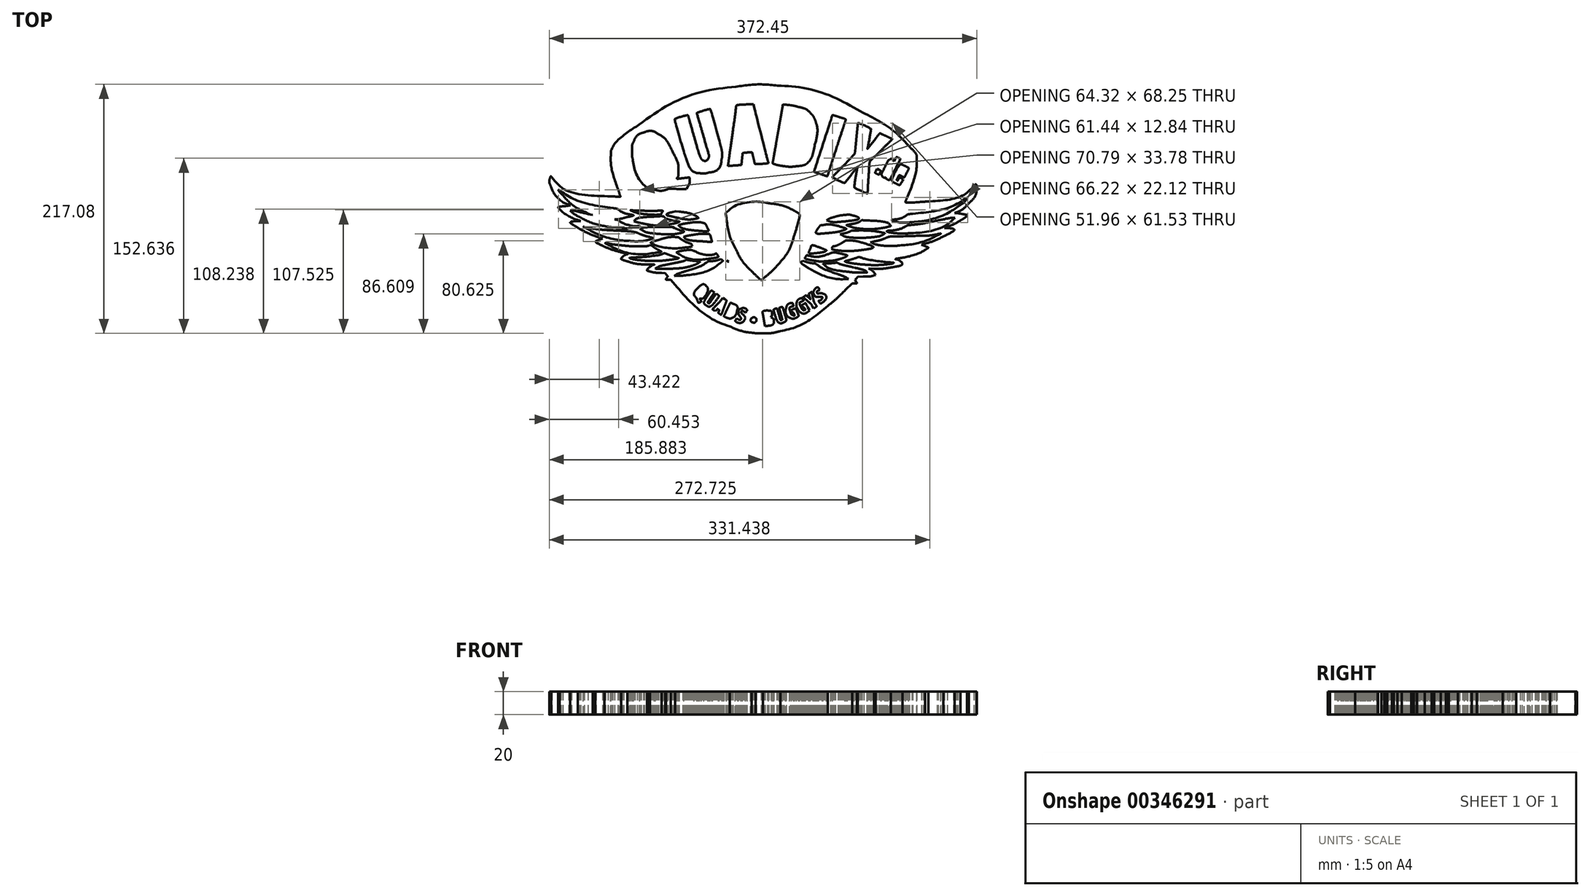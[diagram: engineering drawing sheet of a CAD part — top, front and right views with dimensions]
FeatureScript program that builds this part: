
annotation { "Feature Type Name" : "Feature", "Feature Type Description" : "" }
export const myFeature = defineFeature(function(context is Context, id is Id, definition is map)
    precondition{}
    {
        {
            var Q0;
            Q0=qCreatedBy(makeId("Top.planeOp"),FACE);
            var sketch = newSketch(context, id + "F0", { "sketchPlane" : qUnion([Q0])});
            skFitSpline(sketch, "E0", {"points": [v(-6.57, -108.21) * mm, v(-6.97, -108.16) * mm, v(-8.6, -107.94) * mm, v(-10.17, -107.73) * mm]});
            skFitSpline(sketch, "E1", {"points": [v(-10.17, -107.73) * mm, v(-15.63, -107) * mm, v(-22.77, -104.94) * mm, v(-29.01, -102.3) * mm]});
            skFitSpline(sketch, "E2", {"points": [v(-29.01, -102.3) * mm, v(-44.52, -95.74) * mm, v(-61.29, -82.95) * mm, v(-76.72, -65.93) * mm]});
            skFitSpline(sketch, "E3", {"points": [v(-82.66, -61.55) * mm, v(-83.73, -61.55) * mm, v(-84.68, -61.49) * mm, v(-84.76, -61.4) * mm]});
            skFitSpline(sketch, "E4", {"points": [v(-84.76, -61.4) * mm, v(-84.84, -61.32) * mm, v(-84.54, -60.7) * mm, v(-84.08, -60.03) * mm]});
            skFitSpline(sketch, "E5", {"points": [v(-84.08, -60.03) * mm, v(-83.63, -59.35) * mm, v(-83.25, -58.7) * mm, v(-83.25, -58.6) * mm]});
            skFitSpline(sketch, "E6", {"points": [v(-83.25, -58.6) * mm, v(-83.25, -58.48) * mm, v(-83.74, -57.82) * mm, v(-84.34, -57.12) * mm]});
            skLineSegment(sketch, "E7", {"start": v(-76.72, -65.93) * mm, "end": v(-80.7, -61.55) * mm});
            skLineSegment(sketch, "E8", {"start": v(-80.7, -61.55) * mm, "end": v(-82.66, -61.55) * mm});
            skFitSpline(sketch, "E9", {"points": [v(-88.48, -55.68) * mm, v(-92.46, -55.46) * mm, v(-96.36, -54.96) * mm, v(-98.72, -54.36) * mm]});
            skFitSpline(sketch, "E10", {"points": [v(-98.72, -54.36) * mm, v(-99.76, -54.09) * mm, v(-100.66, -53.83) * mm, v(-100.71, -53.77) * mm]});
            skFitSpline(sketch, "E11", {"points": [v(-100.71, -53.77) * mm, v(-101.28, -53.2) * mm, v(-96.96, -49.12) * mm, v(-95.03, -48.4) * mm]});
            skFitSpline(sketch, "E12", {"points": [v(-95.03, -48.4) * mm, v(-94.78, -48.31) * mm, v(-96.58, -48.22) * mm, v(-99.05, -48.2) * mm]});
            skFitSpline(sketch, "E13", {"points": [v(-99.05, -48.2) * mm, v(-105.73, -48.14) * mm, v(-112.51, -47.22) * mm, v(-118.17, -45.6) * mm]});
            skFitSpline(sketch, "E14", {"points": [v(-118.17, -45.6) * mm, v(-120.5, -44.92) * mm, v(-123.81, -43.47) * mm, v(-123.81, -43.12) * mm]});
            skFitSpline(sketch, "E15", {"points": [v(-123.81, -43.12) * mm, v(-123.81, -43) * mm, v(-123.3, -42.4) * mm, v(-122.65, -41.8) * mm]});
            skFitSpline(sketch, "E16", {"points": [v(-122.65, -41.8) * mm, v(-121.48, -40.72) * mm, v(-120.13, -39.9) * mm, v(-118.57, -39.37) * mm]});
            skFitSpline(sketch, "E17", {"points": [v(-118.57, -39.37) * mm, v(-117.75, -39.08) * mm, v(-117.81, -39.06) * mm, v(-121.43, -38.16) * mm]});
            skFitSpline(sketch, "E18", {"points": [v(-121.43, -38.16) * mm, v(-127.3, -36.7) * mm, v(-133.67, -34.6) * mm, v(-138.21, -32.64) * mm]});
            skFitSpline(sketch, "E19", {"points": [v(-138.21, -32.64) * mm, v(-141.82, -31.08) * mm, v(-146.19, -28.36) * mm, v(-145.73, -27.96) * mm]});
            skFitSpline(sketch, "E20", {"points": [v(-145.73, -27.96) * mm, v(-145.62, -27.86) * mm, v(-144.25, -27.32) * mm, v(-142.68, -26.75) * mm]});
            skLineSegment(sketch, "E21", {"start": v(-84.34, -57.12) * mm, "end": v(-85.42, -55.85) * mm});
            skLineSegment(sketch, "E22", {"start": v(-85.42, -55.85) * mm, "end": v(-88.48, -55.68) * mm});
            skFitSpline(sketch, "E23", {"points": [v(-143.16, -24.6) * mm, v(-145, -23.97) * mm, v(-147.36, -23.12) * mm, v(-148.41, -22.7) * mm]});
            skFitSpline(sketch, "E24", {"points": [v(-148.41, -22.7) * mm, v(-151.53, -21.43) * mm, v(-158.78, -17.84) * mm, v(-161.5, -16.2) * mm]});
            skFitSpline(sketch, "E25", {"points": [v(-161.5, -16.2) * mm, v(-165.45, -13.82) * mm, v(-168.13, -11.68) * mm, v(-167.68, -11.26) * mm]});
            skFitSpline(sketch, "E26", {"points": [v(-167.68, -11.26) * mm, v(-167.32, -10.93) * mm, v(-165.1, -10.61) * mm, v(-162.33, -10.5) * mm]});
            skLineSegment(sketch, "E27", {"start": v(-142.68, -26.75) * mm, "end": v(-139.83, -25.72) * mm});
            skLineSegment(sketch, "E28", {"start": v(-139.83, -25.72) * mm, "end": v(-143.16, -24.6) * mm});
            skFitSpline(sketch, "E29", {"points": [v(-160.17, -9.94) * mm, v(-165.53, -8.08) * mm, v(-174.1, -3.1) * mm, v(-177.45, 0.1) * mm]});
            skFitSpline(sketch, "E30", {"points": [v(-177.45, 0.1) * mm, v(-178.05, 0.67) * mm, v(-178.53, 1.21) * mm, v(-178.53, 1.31) * mm]});
            skFitSpline(sketch, "E31", {"points": [v(-178.53, 1.31) * mm, v(-178.53, 1.66) * mm, v(-173.52, 2.57) * mm, v(-169.82, 2.89) * mm]});
            skLineSegment(sketch, "E32", {"start": v(-162.33, -10.5) * mm, "end": v(-158.97, -10.36) * mm});
            skLineSegment(sketch, "E33", {"start": v(-158.97, -10.36) * mm, "end": v(-160.17, -9.94) * mm});
            skFitSpline(sketch, "E34", {"points": [v(-169.43, 3.76) * mm, v(-174.96, 6.37) * mm, v(-182.09, 13.53) * mm, v(-184.53, 18.93) * mm]});
            skFitSpline(sketch, "E35", {"points": [v(-184.53, 18.93) * mm, v(-185.96, 22.06) * mm, v(-186.33, 25.01) * mm, v(-185.6, 27.44) * mm]});
            skFitSpline(sketch, "E36", {"points": [v(-185.6, 27.44) * mm, v(-185.4, 28.13) * mm, v(-185.15, 28.69) * mm, v(-185.05, 28.69) * mm]});
            skFitSpline(sketch, "E37", {"points": [v(-185.05, 28.69) * mm, v(-184.95, 28.69) * mm, v(-184.45, 28.25) * mm, v(-183.92, 27.7) * mm]});
            skFitSpline(sketch, "E38", {"points": [v(-183.92, 27.7) * mm, v(-174.68, 18.14) * mm, v(-157.86, 12.71) * mm, v(-132.7, 11.17) * mm]});
            skFitSpline(sketch, "E39", {"points": [v(-132.7, 11.17) * mm, v(-130.52, 11.04) * mm, v(-127.72, 10.93) * mm, v(-126.49, 10.93) * mm]});
            skFitSpline(sketch, "E40", {"points": [v(-126.49, 10.93) * mm, v(-124.44, 10.93) * mm, v(-124.26, 10.96) * mm, v(-124.43, 11.35) * mm]});
            skFitSpline(sketch, "E41", {"points": [v(-124.43, 11.35) * mm, v(-124.53, 11.58) * mm, v(-125.51, 14.41) * mm, v(-126.6, 17.65) * mm]});
            skFitSpline(sketch, "E42", {"points": [v(-126.6, 17.65) * mm, v(-130.6, 29.45) * mm, v(-132.7, 39.76) * mm, v(-132.7, 47.68) * mm]});
            skFitSpline(sketch, "E43", {"points": [v(-132.7, 47.68) * mm, v(-132.7, 50.58) * mm, v(-132.66, 50.78) * mm, v(-131.98, 52.07) * mm]});
            skFitSpline(sketch, "E44", {"points": [v(-131.98, 52.07) * mm, v(-129.25, 57.27) * mm, v(-119.8, 65.82) * mm, v(-108.21, 73.56) * mm]});
            skFitSpline(sketch, "E45", {"points": [v(-108.21, 73.56) * mm, v(-82.39, 90.84) * mm, v(-52.34, 102.6) * mm, v(-23.61, 106.67) * mm]});
            skFitSpline(sketch, "E46", {"points": [v(-23.61, 106.67) * mm, v(-11.44, 108.4) * mm, v(0.36, 108.71) * mm, v(12.63, 107.65) * mm]});
            skFitSpline(sketch, "E47", {"points": [v(12.63, 107.65) * mm, v(35.47, 105.67) * mm, v(61.48, 97.6) * mm, v(84.5, 85.35) * mm]});
            skFitSpline(sketch, "E48", {"points": [v(84.5, 85.35) * mm, v(101.82, 76.14) * mm, v(116.2, 65.93) * mm, v(126.16, 55.77) * mm]});
            skFitSpline(sketch, "E49", {"points": [v(126.16, 55.77) * mm, v(131.6, 50.23) * mm, v(133.7, 46.98) * mm, v(133.7, 44.15) * mm]});
            skFitSpline(sketch, "E50", {"points": [v(133.7, 44.15) * mm, v(133.7, 36.24) * mm, v(130.49, 23.07) * mm, v(125.46, 10.4) * mm]});
            skFitSpline(sketch, "E51", {"points": [v(125.46, 10.4) * mm, v(124.58, 8.2) * mm, v(123.87, 6.31) * mm, v(123.87, 6.22) * mm]});
            skFitSpline(sketch, "E52", {"points": [v(123.87, 6.22) * mm, v(123.87, 5.94) * mm, v(138.54, 6.32) * mm, v(143.3, 6.72) * mm]});
            skFitSpline(sketch, "E53", {"points": [v(143.3, 6.72) * mm, v(162.32, 8.32) * mm, v(175.28, 12.72) * mm, v(183.56, 20.38) * mm]});
            skFitSpline(sketch, "E54", {"points": [v(183.56, 20.38) * mm, v(184.38, 21.14) * mm, v(185.15, 21.7) * mm, v(185.28, 21.62) * mm]});
            skFitSpline(sketch, "E55", {"points": [v(185.28, 21.62) * mm, v(185.7, 21.36) * mm, v(186.09, 18.79) * mm, v(185.93, 17.26) * mm]});
            skFitSpline(sketch, "E56", {"points": [v(185.93, 17.26) * mm, v(185.53, 13.36) * mm, v(183.18, 9.18) * mm, v(179.01, 4.95) * mm]});
            skFitSpline(sketch, "E57", {"points": [v(179.01, 4.95) * mm, v(175.48, 1.38) * mm, v(171.2, -1.7) * mm, v(168.17, -2.81) * mm]});
            skLineSegment(sketch, "E58", {"start": v(-169.82, 2.89) * mm, "end": v(-167.95, 3.05) * mm});
            skLineSegment(sketch, "E59", {"start": v(-167.95, 3.05) * mm, "end": v(-169.43, 3.76) * mm});
            skFitSpline(sketch, "E60", {"points": [v(168.7, -3.52) * mm, v(169.79, -3.6) * mm, v(171.3, -3.8) * mm, v(172.05, -3.96) * mm]});
            skFitSpline(sketch, "E61", {"points": [v(172.05, -3.96) * mm, v(175.1, -4.56) * mm, v(177.63, -5.2) * mm, v(177.63, -5.37) * mm]});
            skFitSpline(sketch, "E62", {"points": [v(177.63, -5.37) * mm, v(177.63, -5.87) * mm, v(174.88, -8.01) * mm, v(171.99, -9.77) * mm]});
            skFitSpline(sketch, "E63", {"points": [v(171.99, -9.77) * mm, v(167.65, -12.41) * mm, v(164.93, -13.73) * mm, v(160.27, -15.48) * mm]});
            skLineSegment(sketch, "E64", {"start": v(168.17, -2.81) * mm, "end": v(166.7, -3.35) * mm});
            skLineSegment(sketch, "E65", {"start": v(166.7, -3.35) * mm, "end": v(168.7, -3.52) * mm});
            skFitSpline(sketch, "E66", {"points": [v(160.52, -16.52) * mm, v(163.15, -16.68) * mm, v(165.78, -17.2) * mm, v(166.23, -17.66) * mm]});
            skFitSpline(sketch, "E67", {"points": [v(166.23, -17.66) * mm, v(166.76, -18.2) * mm, v(162.4, -21.1) * mm, v(157, -23.77) * mm]});
            skFitSpline(sketch, "E68", {"points": [v(157, -23.77) * mm, v(151.4, -26.55) * mm, v(145.67, -28.76) * mm, v(139.48, -30.53) * mm]});
            skLineSegment(sketch, "E69", {"start": v(160.27, -15.48) * mm, "end": v(157.91, -16.36) * mm});
            skLineSegment(sketch, "E70", {"start": v(157.91, -16.36) * mm, "end": v(160.52, -16.52) * mm});
            skFitSpline(sketch, "E71", {"points": [v(140.8, -32.14) * mm, v(142.38, -32.79) * mm, v(143.72, -33.36) * mm, v(143.79, -33.42) * mm]});
            skFitSpline(sketch, "E72", {"points": [v(143.79, -33.42) * mm, v(143.98, -33.58) * mm, v(142.58, -34.63) * mm, v(140.92, -35.57) * mm]});
            skFitSpline(sketch, "E73", {"points": [v(140.92, -35.57) * mm, v(136.46, -38.1) * mm, v(126, -41.44) * mm, v(117.82, -42.96) * mm]});
            skFitSpline(sketch, "E74", {"points": [v(117.82, -42.96) * mm, v(115.47, -43.4) * mm, v(115.15, -43.6) * mm, v(116.36, -43.9) * mm]});
            skFitSpline(sketch, "E75", {"points": [v(116.36, -43.9) * mm, v(117.78, -44.25) * mm, v(121.1, -46.9) * mm, v(121.1, -47.67) * mm]});
            skFitSpline(sketch, "E76", {"points": [v(121.1, -47.67) * mm, v(121.1, -48.47) * mm, v(116.4, -50) * mm, v(111.27, -50.87) * mm]});
            skFitSpline(sketch, "E77", {"points": [v(111.27, -50.87) * mm, v(106.35, -51.7) * mm, v(101.4, -52.04) * mm, v(96.34, -51.9) * mm]});
            skLineSegment(sketch, "E78", {"start": v(139.48, -30.53) * mm, "end": v(137.94, -30.97) * mm});
            skLineSegment(sketch, "E79", {"start": v(137.94, -30.97) * mm, "end": v(140.8, -32.14) * mm});
            skFitSpline(sketch, "E80", {"points": [v(93.19, -52.5) * mm, v(94.6, -53.3) * mm, v(96.87, -55.5) * mm, v(97.53, -56.69) * mm]});
            skLineSegment(sketch, "E81", {"start": v(96.34, -51.9) * mm, "end": v(91.92, -51.78) * mm});
            skLineSegment(sketch, "E82", {"start": v(91.92, -51.78) * mm, "end": v(93.19, -52.5) * mm});
            skFitSpline(sketch, "E83", {"points": [v(96.7, -57.82) * mm, v(94.52, -58.45) * mm, v(92.23, -58.7) * mm, v(87.22, -58.84) * mm]});
            skLineSegment(sketch, "E84", {"start": v(97.53, -56.69) * mm, "end": v(97.96, -57.45) * mm});
            skLineSegment(sketch, "E85", {"start": v(97.96, -57.45) * mm, "end": v(96.7, -57.82) * mm});
            skFitSpline(sketch, "E86", {"points": [v(80.86, -63.01) * mm, v(81.28, -63.78) * mm, v(81.63, -64.46) * mm, v(81.63, -64.54) * mm]});
            skFitSpline(sketch, "E87", {"points": [v(81.63, -64.54) * mm, v(81.63, -64.61) * mm, v(80.68, -64.67) * mm, v(79.53, -64.67) * mm]});
            skLineSegment(sketch, "E88", {"start": v(87.22, -58.84) * mm, "end": v(82.38, -58.98) * mm});
            skLineSegment(sketch, "E89", {"start": v(82.38, -58.98) * mm, "end": v(81.23, -60.3) * mm});
            skLineSegment(sketch, "E90", {"start": v(81.23, -60.3) * mm, "end": v(80.1, -61.63) * mm});
            skLineSegment(sketch, "E91", {"start": v(80.1, -61.63) * mm, "end": v(80.86, -63.01) * mm});
            skFitSpline(sketch, "E92", {"points": [v(71.55, -70.5) * mm, v(65.32, -76.67) * mm, v(61.44, -80.17) * mm, v(56.23, -84.33) * mm]});
            skFitSpline(sketch, "E93", {"points": [v(56.23, -84.33) * mm, v(42.35, -95.39) * mm, v(28.04, -103) * mm, v(14.93, -106.3) * mm]});
            skFitSpline(sketch, "E94", {"points": [v(14.93, -106.3) * mm, v(9.4, -107.7) * mm, v(5.85, -108.16) * mm, v(-0.21, -108.24) * mm]});
            skFitSpline(sketch, "E95", {"points": [v(-0.21, -108.24) * mm, v(-3.32, -108.28) * mm, v(-6.18, -108.27) * mm, v(-6.57, -108.21) * mm]});
            skLineSegment(sketch, "E96", {"start": v(79.53, -64.67) * mm, "end": v(77.43, -64.68) * mm});
            skLineSegment(sketch, "E97", {"start": v(77.43, -64.68) * mm, "end": v(71.55, -70.5) * mm});
            skFitSpline(sketch, "E98", {"points": [v(4.95, -101.6) * mm, v(7.46, -101.13) * mm, v(9.15, -99.57) * mm, v(9.15, -97.73) * mm]});
            skFitSpline(sketch, "E99", {"points": [v(9.15, -97.73) * mm, v(9.15, -96.34) * mm, v(8.5, -95.16) * mm, v(7.47, -94.7) * mm]});
            skLineSegment(sketch, "E100", {"start": v(-6.57, -108.21) * mm, "end": v(-6.57, -108.21) * mm});
            skFitSpline(sketch, "E101", {"points": [v(7.18, -93.47) * mm, v(7.65, -92.78) * mm, v(7.73, -92.41) * mm, v(7.65, -91.36) * mm]});
            skFitSpline(sketch, "E102", {"points": [v(7.65, -91.36) * mm, v(7.5, -89.53) * mm, v(6.58, -88.64) * mm, v(4.69, -88.48) * mm]});
            skFitSpline(sketch, "E103", {"points": [v(4.69, -88.48) * mm, v(3.32, -88.37) * mm, v(0.42, -88.76) * mm, v(-0.2, -89.14) * mm]});
            skFitSpline(sketch, "E104", {"points": [v(-0.2, -89.14) * mm, v(-0.51, -89.34) * mm, v(-0.06, -92.94) * mm, v(1.26, -100.62) * mm]});
            skLineSegment(sketch, "E105", {"start": v(7.47, -94.7) * mm, "end": v(6.6, -94.31) * mm});
            skLineSegment(sketch, "E106", {"start": v(6.6, -94.31) * mm, "end": v(7.18, -93.47) * mm});
            skFitSpline(sketch, "E107", {"points": [v(2.63, -101.99) * mm, v(3.24, -101.9) * mm, v(4.29, -101.74) * mm, v(4.95, -101.6) * mm]});
            skLineSegment(sketch, "E108", {"start": v(1.26, -100.62) * mm, "end": v(1.52, -102.13) * mm});
            skLineSegment(sketch, "E109", {"start": v(1.52, -102.13) * mm, "end": v(2.63, -101.99) * mm});
            skFitSpline(sketch, "E110", {"points": [v(17.64, -98.8) * mm, v(19.8, -97.55) * mm, v(19.91, -95.56) * mm, v(18.16, -89.45) * mm]});
            skFitSpline(sketch, "E111", {"points": [v(18.16, -89.45) * mm, v(17.5, -87.18) * mm, v(16.87, -85.31) * mm, v(16.75, -85.31) * mm]});
            skFitSpline(sketch, "E112", {"points": [v(16.75, -85.31) * mm, v(16.28, -85.31) * mm, v(13.95, -86.08) * mm, v(13.95, -86.23) * mm]});
            skFitSpline(sketch, "E113", {"points": [v(13.95, -86.23) * mm, v(13.95, -86.32) * mm, v(14.53, -88.44) * mm, v(15.24, -90.95) * mm]});
            skFitSpline(sketch, "E114", {"points": [v(15.24, -90.95) * mm, v(16.54, -95.52) * mm, v(16.62, -96.38) * mm, v(15.8, -96.55) * mm]});
            skFitSpline(sketch, "E115", {"points": [v(15.8, -96.55) * mm, v(15.16, -96.67) * mm, v(14.71, -95.65) * mm, v(13.42, -91.17) * mm]});
            skFitSpline(sketch, "E116", {"points": [v(13.42, -91.17) * mm, v(12.74, -88.8) * mm, v(12.14, -86.83) * mm, v(12.1, -86.77) * mm]});
            skFitSpline(sketch, "E117", {"points": [v(12.1, -86.77) * mm, v(11.96, -86.59) * mm, v(9.34, -87.32) * mm, v(9.24, -87.58) * mm]});
            skFitSpline(sketch, "E118", {"points": [v(9.24, -87.58) * mm, v(9.1, -87.95) * mm, v(11.4, -95.83) * mm, v(11.97, -96.96) * mm]});
            skFitSpline(sketch, "E119", {"points": [v(11.97, -96.96) * mm, v(12.53, -98.05) * mm, v(13.32, -98.85) * mm, v(14.19, -99.21) * mm]});
            skFitSpline(sketch, "E120", {"points": [v(14.19, -99.21) * mm, v(14.95, -99.53) * mm, v(16.74, -99.31) * mm, v(17.64, -98.8) * mm]});
            skFitSpline(sketch, "E121", {"points": [v(-18.2, -98.68) * mm, v(-17.5, -98.3) * mm, v(-16.99, -97.8) * mm, v(-16.6, -97.08) * mm]});
            skFitSpline(sketch, "E122", {"points": [v(-16.6, -97.08) * mm, v(-15.66, -95.3) * mm, v(-15.94, -93.78) * mm, v(-17.6, -91.82) * mm]});
            skFitSpline(sketch, "E123", {"points": [v(-17.6, -91.82) * mm, v(-19.17, -89.94) * mm, v(-18.31, -88.63) * mm, v(-16.23, -89.73) * mm]});
            skFitSpline(sketch, "E124", {"points": [v(-14.54, -89.16) * mm, v(-13.94, -88.07) * mm, v(-13.92, -88) * mm, v(-14.33, -87.63) * mm]});
            skFitSpline(sketch, "E125", {"points": [v(-14.33, -87.63) * mm, v(-15.54, -86.54) * mm, v(-18.06, -86.19) * mm, v(-19.57, -86.9) * mm]});
            skFitSpline(sketch, "E126", {"points": [v(-19.57, -86.9) * mm, v(-20.72, -87.45) * mm, v(-21.57, -88.99) * mm, v(-21.57, -90.51) * mm]});
            skFitSpline(sketch, "E127", {"points": [v(-21.57, -90.51) * mm, v(-21.57, -91.52) * mm, v(-21.42, -91.93) * mm, v(-20.63, -93.07) * mm]});
            skFitSpline(sketch, "E128", {"points": [v(-20.63, -93.07) * mm, v(-19.22, -95.07) * mm, v(-19.12, -95.32) * mm, v(-19.41, -95.87) * mm]});
            skFitSpline(sketch, "E129", {"points": [v(-19.41, -95.87) * mm, v(-19.77, -96.54) * mm, v(-20.94, -96.5) * mm, v(-22.2, -95.75) * mm]});
            skLineSegment(sketch, "E130", {"start": v(-16.23, -89.73) * mm, "end": v(-15.18, -90.3) * mm});
            skLineSegment(sketch, "E131", {"start": v(-15.18, -90.3) * mm, "end": v(-14.54, -89.16) * mm});
            skFitSpline(sketch, "E132", {"points": [v(-23.84, -96.32) * mm, v(-24.43, -97.48) * mm, v(-24.43, -97.5) * mm, v(-23.97, -97.92) * mm]});
            skFitSpline(sketch, "E133", {"points": [v(-23.97, -97.92) * mm, v(-23.34, -98.49) * mm, v(-21.19, -99.21) * mm, v(-20.11, -99.22) * mm]});
            skFitSpline(sketch, "E134", {"points": [v(-20.11, -99.22) * mm, v(-19.64, -99.23) * mm, v(-18.78, -98.98) * mm, v(-18.2, -98.68) * mm]});
            skLineSegment(sketch, "E135", {"start": v(-22.2, -95.75) * mm, "end": v(-23.24, -95.14) * mm});
            skLineSegment(sketch, "E136", {"start": v(-23.24, -95.14) * mm, "end": v(-23.84, -96.32) * mm});
            skFitSpline(sketch, "E137", {"points": [v(-6.71, -98.37) * mm, v(-6.08, -97.84) * mm, v(-5.97, -97.6) * mm, v(-5.97, -96.59) * mm]});
            skFitSpline(sketch, "E138", {"points": [v(-5.97, -96.59) * mm, v(-5.97, -95.62) * mm, v(-6.08, -95.34) * mm, v(-6.6, -94.93) * mm]});
            skFitSpline(sketch, "E139", {"points": [v(-6.6, -94.93) * mm, v(-7.31, -94.37) * mm, v(-8.75, -94.27) * mm, v(-9.36, -94.74) * mm]});
            skFitSpline(sketch, "E140", {"points": [v(-9.36, -94.74) * mm, v(-10.72, -95.8) * mm, v(-10.52, -98.14) * mm, v(-9, -98.75) * mm]});
            skFitSpline(sketch, "E141", {"points": [v(-9, -98.75) * mm, v(-8.11, -99.12) * mm, v(-7.47, -99.01) * mm, v(-6.71, -98.37) * mm]});
            skFitSpline(sketch, "E142", {"points": [v(-26.9, -94.74) * mm, v(-25.3, -93.98) * mm, v(-23.31, -90.9) * mm, v(-22.78, -88.32) * mm]});
            skFitSpline(sketch, "E143", {"points": [v(-22.78, -88.32) * mm, v(-22.24, -85.76) * mm, v(-23.35, -83.9) * mm, v(-26.25, -82.52) * mm]});
            skFitSpline(sketch, "E144", {"points": [v(-26.25, -82.52) * mm, v(-27.17, -82.07) * mm, v(-28.1, -81.71) * mm, v(-28.31, -81.71) * mm]});
            skFitSpline(sketch, "E145", {"points": [v(-28.31, -81.71) * mm, v(-28.58, -81.71) * mm, v(-29.53, -83.42) * mm, v(-31.42, -87.33) * mm]});
            skFitSpline(sketch, "E146", {"points": [v(-31.42, -87.33) * mm, v(-32.9, -90.43) * mm, v(-34.14, -93.04) * mm, v(-34.15, -93.15) * mm]});
            skFitSpline(sketch, "E147", {"points": [v(-34.15, -93.15) * mm, v(-34.18, -93.44) * mm, v(-31.72, -94.72) * mm, v(-30.45, -95.07) * mm]});
            skFitSpline(sketch, "E148", {"points": [v(-30.45, -95.07) * mm, v(-29.25, -95.4) * mm, v(-28.1, -95.3) * mm, v(-26.9, -94.74) * mm]});
            skFitSpline(sketch, "E149", {"points": [v(28.91, -94.56) * mm, v(29.66, -94.18) * mm, v(30.39, -93.74) * mm, v(30.52, -93.57) * mm]});
            skFitSpline(sketch, "E150", {"points": [v(30.52, -93.57) * mm, v(30.82, -93.21) * mm, v(28.18, -86.75) * mm, v(27.74, -86.75) * mm]});
            skFitSpline(sketch, "E151", {"points": [v(27.74, -86.75) * mm, v(27.47, -86.75) * mm, v(24.74, -87.89) * mm, v(24.54, -88.08) * mm]});
            skFitSpline(sketch, "E152", {"points": [v(24.54, -88.08) * mm, v(24.5, -88.13) * mm, v(24.65, -88.66) * mm, v(24.88, -89.27) * mm]});
            skFitSpline(sketch, "E153", {"points": [v(24.88, -89.27) * mm, v(25.23, -90.2) * mm, v(25.39, -90.36) * mm, v(25.8, -90.26) * mm]});
            skFitSpline(sketch, "E154", {"points": [v(25.8, -90.26) * mm, v(26.22, -90.15) * mm, v(26.39, -90.32) * mm, v(26.76, -91.23) * mm]});
            skFitSpline(sketch, "E155", {"points": [v(26.76, -91.23) * mm, v(27.29, -92.5) * mm, v(27.04, -92.86) * mm, v(25.9, -92.46) * mm]});
            skFitSpline(sketch, "E156", {"points": [v(25.9, -92.46) * mm, v(24.95, -92.13) * mm, v(23.98, -90.74) * mm, v(23.43, -88.94) * mm]});
            skFitSpline(sketch, "E157", {"points": [v(23.43, -88.94) * mm, v(22.83, -86.93) * mm, v(23.15, -85.76) * mm, v(24.5, -85.07) * mm]});
            skFitSpline(sketch, "E158", {"points": [v(24.5, -85.07) * mm, v(25.02, -84.8) * mm, v(25.61, -84.6) * mm, v(25.82, -84.6) * mm]});
            skFitSpline(sketch, "E159", {"points": [v(25.82, -84.6) * mm, v(26.25, -84.6) * mm, v(26.28, -84.1) * mm, v(25.93, -82.85) * mm]});
            skFitSpline(sketch, "E160", {"points": [v(25.93, -82.85) * mm, v(25.72, -82.1) * mm, v(25.58, -81.95) * mm, v(25.03, -81.95) * mm]});
            skFitSpline(sketch, "E161", {"points": [v(25.03, -81.95) * mm, v(23.18, -81.96) * mm, v(20.67, -84) * mm, v(20.15, -85.91) * mm]});
            skFitSpline(sketch, "E162", {"points": [v(20.15, -85.91) * mm, v(19.33, -88.95) * mm, v(21.23, -93.57) * mm, v(23.85, -94.9) * mm]});
            skFitSpline(sketch, "E163", {"points": [v(23.85, -94.9) * mm, v(25.24, -95.6) * mm, v(27.08, -95.48) * mm, v(28.91, -94.56) * mm]});
            skFitSpline(sketch, "E164", {"points": [v(-34.32, -86.25) * mm, v(-33.12, -83.06) * mm, v(-32.08, -80.23) * mm, v(-32, -79.95) * mm]});
            skFitSpline(sketch, "E165", {"points": [v(-32, -79.95) * mm, v(-31.9, -79.52) * mm, v(-32.15, -79.28) * mm, v(-33.46, -78.52) * mm]});
            skFitSpline(sketch, "E166", {"points": [v(-37.02, -79.72) * mm, v(-42.27, -85.32) * mm, v(-44.13, -87.35) * mm, v(-44.13, -87.47) * mm]});
            skFitSpline(sketch, "E167", {"points": [v(-44.13, -87.47) * mm, v(-44.13, -87.54) * mm, v(-43.58, -87.9) * mm, v(-42.91, -88.28) * mm]});
            skLineSegment(sketch, "E168", {"start": v(-33.46, -78.52) * mm, "end": v(-35.04, -77.6) * mm});
            skLineSegment(sketch, "E169", {"start": v(-35.04, -77.6) * mm, "end": v(-37.02, -79.72) * mm});
            skFitSpline(sketch, "E170", {"points": [v(-40.8, -88.1) * mm, v(-39.79, -87.1) * mm, v(-39.67, -87.08) * mm, v(-38.88, -87.68) * mm]});
            skFitSpline(sketch, "E171", {"points": [v(-38.88, -87.68) * mm, v(-38.31, -88.12) * mm, v(-38.3, -88.13) * mm, v(-38.7, -89.28) * mm]});
            skFitSpline(sketch, "E172", {"points": [v(-38.7, -89.28) * mm, v(-38.92, -89.91) * mm, v(-39.03, -90.5) * mm, v(-38.95, -90.57) * mm]});
            skFitSpline(sketch, "E173", {"points": [v(-38.95, -90.57) * mm, v(-38.73, -90.8) * mm, v(-36.83, -92) * mm, v(-36.67, -92.02) * mm]});
            skFitSpline(sketch, "E174", {"points": [v(-36.67, -92.02) * mm, v(-36.58, -92.03) * mm, v(-35.53, -89.43) * mm, v(-34.32, -86.25) * mm]});
            skLineSegment(sketch, "E175", {"start": v(-42.91, -88.28) * mm, "end": v(-41.69, -88.97) * mm});
            skLineSegment(sketch, "E176", {"start": v(-41.69, -88.97) * mm, "end": v(-40.8, -88.1) * mm});
            skFitSpline(sketch, "E177", {"points": [v(37.6, -90.38) * mm, v(38.14, -90.14) * mm, v(38.97, -89.59) * mm, v(39.46, -89.16) * mm]});
            skFitSpline(sketch, "E178", {"points": [v(38.84, -85.6) * mm, v(38.02, -84.05) * mm, v(37.23, -82.6) * mm, v(37.1, -82.37) * mm]});
            skFitSpline(sketch, "E179", {"points": [v(37.1, -82.37) * mm, v(36.87, -81.99) * mm, v(36.72, -82.02) * mm, v(35.24, -82.8) * mm]});
            skFitSpline(sketch, "E180", {"points": [v(35.24, -82.8) * mm, v(34.35, -83.28) * mm, v(33.63, -83.7) * mm, v(33.63, -83.76) * mm]});
            skFitSpline(sketch, "E181", {"points": [v(33.63, -83.76) * mm, v(33.63, -83.82) * mm, v(33.86, -84.34) * mm, v(34.15, -84.93) * mm]});
            skFitSpline(sketch, "E182", {"points": [v(34.15, -84.93) * mm, v(34.58, -85.82) * mm, v(34.74, -85.97) * mm, v(35.09, -85.78) * mm]});
            skFitSpline(sketch, "E183", {"points": [v(35.09, -85.78) * mm, v(35.43, -85.6) * mm, v(35.62, -85.75) * mm, v(36.13, -86.67) * mm]});
            skFitSpline(sketch, "E184", {"points": [v(36.13, -86.67) * mm, v(36.8, -87.87) * mm, v(36.8, -87.88) * mm, v(36.27, -87.96) * mm]});
            skFitSpline(sketch, "E185", {"points": [v(36.27, -87.96) * mm, v(34.97, -88.14) * mm, v(33.82, -87.2) * mm, v(32.87, -85.2) * mm]});
            skFitSpline(sketch, "E186", {"points": [v(32.87, -85.2) * mm, v(31.72, -82.78) * mm, v(32.02, -81.34) * mm, v(33.84, -80.48) * mm]});
            skFitSpline(sketch, "E187", {"points": [v(33.84, -80.48) * mm, v(34.45, -80.19) * mm, v(34.97, -79.94) * mm, v(35, -79.91) * mm]});
            skFitSpline(sketch, "E188", {"points": [v(35, -79.91) * mm, v(35.07, -79.87) * mm, v(34.33, -77.58) * mm, v(34.2, -77.43) * mm]});
            skFitSpline(sketch, "E189", {"points": [v(34.2, -77.43) * mm, v(34.17, -77.38) * mm, v(33.57, -77.53) * mm, v(32.88, -77.76) * mm]});
            skFitSpline(sketch, "E190", {"points": [v(32.88, -77.76) * mm, v(31.38, -78.26) * mm, v(29.74, -79.8) * mm, v(29.31, -81.1) * mm]});
            skFitSpline(sketch, "E191", {"points": [v(29.31, -81.1) * mm, v(28.86, -82.47) * mm, v(29.1, -84.96) * mm, v(29.83, -86.54) * mm]});
            skFitSpline(sketch, "E192", {"points": [v(29.83, -86.54) * mm, v(30.57, -88.14) * mm, v(31.94, -89.73) * mm, v(33.13, -90.36) * mm]});
            skFitSpline(sketch, "E193", {"points": [v(33.13, -90.36) * mm, v(34.25, -90.95) * mm, v(36.32, -90.96) * mm, v(37.6, -90.38) * mm]});
            skLineSegment(sketch, "E194", {"start": v(39.46, -89.16) * mm, "end": v(40.34, -88.39) * mm});
            skLineSegment(sketch, "E195", {"start": v(40.34, -88.39) * mm, "end": v(38.84, -85.6) * mm});
            skFitSpline(sketch, "E196", {"points": [v(46.17, -85.2) * mm, v(46.4, -85.07) * mm, v(46.59, -84.88) * mm, v(46.59, -84.78) * mm]});
            skFitSpline(sketch, "E197", {"points": [v(46.59, -84.78) * mm, v(46.59, -84.69) * mm, v(46.03, -83.74) * mm, v(45.36, -82.67) * mm]});
            skFitSpline(sketch, "E198", {"points": [v(45.36, -82.67) * mm, v(44.2, -80.86) * mm, v(44.07, -80.48) * mm, v(43.19, -76.5) * mm]});
            skFitSpline(sketch, "E199", {"points": [v(43.19, -76.5) * mm, v(42.67, -74.16) * mm, v(42.22, -72.23) * mm, v(42.2, -72.2) * mm]});
            skFitSpline(sketch, "E200", {"points": [v(42.2, -72.2) * mm, v(42.16, -72.17) * mm, v(41.52, -72.52) * mm, v(40.77, -72.98) * mm]});
            skFitSpline(sketch, "E201", {"points": [v(40.1, -75.67) * mm, v(40.47, -76.68) * mm, v(40.89, -77.79) * mm, v(41.02, -78.13) * mm]});
            skFitSpline(sketch, "E202", {"points": [v(41.02, -78.13) * mm, v(41.2, -78.57) * mm, v(40.74, -78.24) * mm, v(39.42, -76.99) * mm]});
            skFitSpline(sketch, "E203", {"points": [v(39.42, -76.99) * mm, v(38.41, -76.02) * mm, v(37.48, -75.24) * mm, v(37.35, -75.24) * mm]});
            skFitSpline(sketch, "E204", {"points": [v(37.35, -75.24) * mm, v(37.21, -75.24) * mm, v(36.54, -75.6) * mm, v(35.84, -76.05) * mm]});
            skLineSegment(sketch, "E205", {"start": v(40.77, -72.98) * mm, "end": v(39.4, -73.82) * mm});
            skLineSegment(sketch, "E206", {"start": v(39.4, -73.82) * mm, "end": v(40.1, -75.67) * mm});
            skFitSpline(sketch, "E207", {"points": [v(38.06, -79.66) * mm, v(41.2, -82.2) * mm, v(41.66, -82.67) * mm, v(42.77, -84.5) * mm]});
            skLineSegment(sketch, "E208", {"start": v(35.84, -76.05) * mm, "end": v(34.58, -76.85) * mm});
            skLineSegment(sketch, "E209", {"start": v(34.58, -76.85) * mm, "end": v(38.06, -79.66) * mm});
            skFitSpline(sketch, "E210", {"points": [v(44.88, -85.99) * mm, v(45.35, -85.7) * mm, v(45.93, -85.35) * mm, v(46.17, -85.2) * mm]});
            skLineSegment(sketch, "E211", {"start": v(42.77, -84.5) * mm, "end": v(44, -86.51) * mm});
            skLineSegment(sketch, "E212", {"start": v(44, -86.51) * mm, "end": v(44.88, -85.99) * mm});
            skFitSpline(sketch, "E213", {"points": [v(-45.39, -84.38) * mm, v(-44.9, -84.12) * mm, v(-44.26, -83.67) * mm, v(-43.98, -83.36) * mm]});
            skFitSpline(sketch, "E214", {"points": [v(-43.98, -83.36) * mm, v(-42.97, -82.25) * mm, v(-38.4, -75.62) * mm, v(-38.52, -75.43) * mm]});
            skFitSpline(sketch, "E215", {"points": [v(-38.52, -75.43) * mm, v(-38.59, -75.33) * mm, v(-39.14, -74.9) * mm, v(-39.75, -74.48) * mm]});
            skFitSpline(sketch, "E216", {"points": [v(-41.28, -74.25) * mm, v(-41.52, -74.54) * mm, v(-42.8, -76.33) * mm, v(-44.13, -78.23) * mm]});
            skFitSpline(sketch, "E217", {"points": [v(-44.13, -78.23) * mm, v(-46.37, -81.45) * mm, v(-47.13, -82.2) * mm, v(-47.73, -81.83) * mm]});
            skFitSpline(sketch, "E218", {"points": [v(-47.73, -81.83) * mm, v(-48.26, -81.51) * mm, v(-47.92, -80.5) * mm, v(-46.71, -78.74) * mm]});
            skFitSpline(sketch, "E219", {"points": [v(-46.71, -78.74) * mm, v(-46.02, -77.74) * mm, v(-44.78, -75.95) * mm, v(-43.96, -74.77) * mm]});
            skLineSegment(sketch, "E220", {"start": v(-39.75, -74.48) * mm, "end": v(-40.85, -73.72) * mm});
            skLineSegment(sketch, "E221", {"start": v(-40.85, -73.72) * mm, "end": v(-41.28, -74.25) * mm});
            skFitSpline(sketch, "E222", {"points": [v(-43.65, -71.75) * mm, v(-44.3, -71.27) * mm, v(-44.95, -70.94) * mm, v(-45.07, -71.02) * mm]});
            skFitSpline(sketch, "E223", {"points": [v(-45.07, -71.02) * mm, v(-45.49, -71.27) * mm, v(-50.15, -78.1) * mm, v(-50.62, -79.13) * mm]});
            skFitSpline(sketch, "E224", {"points": [v(-50.62, -79.13) * mm, v(-51.57, -81.22) * mm, v(-51.1, -82.85) * mm, v(-49.16, -84.15) * mm]});
            skFitSpline(sketch, "E225", {"points": [v(-49.16, -84.15) * mm, v(-47.94, -84.97) * mm, v(-46.68, -85.04) * mm, v(-45.39, -84.38) * mm]});
            skLineSegment(sketch, "E226", {"start": v(-43.96, -74.77) * mm, "end": v(-42.46, -72.63) * mm});
            skLineSegment(sketch, "E227", {"start": v(-42.46, -72.63) * mm, "end": v(-43.65, -71.75) * mm});
            skFitSpline(sketch, "E228", {"points": [v(51.57, -81.46) * mm, v(52.26, -81.06) * mm, v(53.15, -80.3) * mm, v(53.55, -79.75) * mm]});
            skFitSpline(sketch, "E229", {"points": [v(53.55, -79.75) * mm, v(55, -77.73) * mm, v(54.3, -74.91) * mm, v(52.05, -73.76) * mm]});
            skFitSpline(sketch, "E230", {"points": [v(52.05, -73.76) * mm, v(51.23, -73.35) * mm, v(50.77, -73.28) * mm, v(49.52, -73.38) * mm]});
            skFitSpline(sketch, "E231", {"points": [v(49.52, -73.38) * mm, v(47.6, -73.53) * mm, v(47.1, -73.4) * mm, v(46.91, -72.67) * mm]});
            skFitSpline(sketch, "E232", {"points": [v(46.91, -72.67) * mm, v(46.73, -71.96) * mm, v(47.3, -71.27) * mm, v(48.4, -70.87) * mm]});
            skFitSpline(sketch, "E233", {"points": [v(48.6, -69.43) * mm, v(48.28, -68.8) * mm, v(47.85, -68.27) * mm, v(47.65, -68.27) * mm]});
            skFitSpline(sketch, "E234", {"points": [v(47.65, -68.27) * mm, v(46.77, -68.27) * mm, v(44.92, -69.76) * mm, v(44.28, -70.96) * mm]});
            skFitSpline(sketch, "E235", {"points": [v(44.28, -70.96) * mm, v(43.75, -71.97) * mm, v(43.85, -73.82) * mm, v(44.49, -74.76) * mm]});
            skFitSpline(sketch, "E236", {"points": [v(44.49, -74.76) * mm, v(45.4, -76.12) * mm, v(46.42, -76.55) * mm, v(48.68, -76.56) * mm]});
            skFitSpline(sketch, "E237", {"points": [v(48.68, -76.56) * mm, v(51, -76.56) * mm, v(51.64, -76.92) * mm, v(51.25, -78.03) * mm]});
            skFitSpline(sketch, "E238", {"points": [v(51.25, -78.03) * mm, v(51.06, -78.58) * mm, v(49.8, -79.48) * mm, v(48.73, -79.84) * mm]});
            skFitSpline(sketch, "E239", {"points": [v(48.73, -79.84) * mm, v(48.4, -79.95) * mm, v(49.64, -82.2) * mm, v(50.03, -82.2) * mm]});
            skFitSpline(sketch, "E240", {"points": [v(50.03, -82.2) * mm, v(50.18, -82.19) * mm, v(50.87, -81.86) * mm, v(51.57, -81.46) * mm]});
            skLineSegment(sketch, "E241", {"start": v(48.4, -70.87) * mm, "end": v(49.2, -70.59) * mm});
            skLineSegment(sketch, "E242", {"start": v(49.2, -70.59) * mm, "end": v(48.6, -69.43) * mm});
            skFitSpline(sketch, "E243", {"points": [v(-55.1, -81.2) * mm, v(-54.55, -80.92) * mm, v(-54.05, -80.66) * mm, v(-54, -80.61) * mm]});
            skFitSpline(sketch, "E244", {"points": [v(-54, -80.61) * mm, v(-53.96, -80.57) * mm, v(-54.2, -80.05) * mm, v(-54.55, -79.46) * mm]});
            skFitSpline(sketch, "E245", {"points": [v(-54.55, -79.46) * mm, v(-55.31, -78.15) * mm, v(-55.32, -78.11) * mm, v(-54.6, -78.11) * mm]});
            skFitSpline(sketch, "E246", {"points": [v(-54.6, -78.11) * mm, v(-53.21, -78.11) * mm, v(-50.1, -75.12) * mm, v(-48.9, -72.62) * mm]});
            skFitSpline(sketch, "E247", {"points": [v(-48.9, -72.62) * mm, v(-48.25, -71.3) * mm, v(-48.06, -69.47) * mm, v(-48.46, -68.51) * mm]});
            skFitSpline(sketch, "E248", {"points": [v(-48.46, -68.51) * mm, v(-48.62, -68.11) * mm, v(-49.07, -67.52) * mm, v(-49.46, -67.2) * mm]});
            skFitSpline(sketch, "E249", {"points": [v(-49.46, -67.2) * mm, v(-51.4, -65.56) * mm, v(-53.72, -65.94) * mm, v(-56.25, -68.3) * mm]});
            skFitSpline(sketch, "E250", {"points": [v(-56.25, -68.3) * mm, v(-59.11, -70.98) * mm, v(-60.28, -74.5) * mm, v(-59, -76.58) * mm]});
            skFitSpline(sketch, "E251", {"points": [v(-59, -76.58) * mm, v(-58.72, -77.03) * mm, v(-58.4, -77.4) * mm, v(-58.3, -77.4) * mm]});
            skFitSpline(sketch, "E252", {"points": [v(-58.3, -77.4) * mm, v(-58.18, -77.4) * mm, v(-58.01, -77.64) * mm, v(-57.92, -77.93) * mm]});
            skFitSpline(sketch, "E253", {"points": [v(-57.92, -77.93) * mm, v(-57.67, -78.73) * mm, v(-56.33, -81.71) * mm, v(-56.21, -81.71) * mm]});
            skFitSpline(sketch, "E254", {"points": [v(-56.21, -81.71) * mm, v(-56.16, -81.71) * mm, v(-55.66, -81.48) * mm, v(-55.1, -81.2) * mm]});
            skLineSegment(sketch, "E255", {"start": v(-55.1, -81.2) * mm, "end": v(-55.1, -81.2) * mm});
            skFitSpline(sketch, "E256", {"points": [v(51.63, -62.9) * mm, v(51.63, -62.77) * mm, v(45.7, -58.06) * mm, v(43.1, -56.12) * mm]});
            skFitSpline(sketch, "E257", {"points": [v(43.1, -56.12) * mm, v(36.69, -51.31) * mm, v(31.06, -47.84) * mm, v(28, -46.81) * mm]});
            skFitSpline(sketch, "E258", {"points": [v(28, -46.81) * mm, v(27.64, -46.69) * mm, v(27.9, -46.43) * mm, v(29.36, -45.47) * mm]});
            skFitSpline(sketch, "E259", {"points": [v(29.36, -45.47) * mm, v(35.03, -41.75) * mm, v(37.94, -35.32) * mm, v(37.95, -26.51) * mm]});
            skFitSpline(sketch, "E260", {"points": [v(37.95, -26.51) * mm, v(37.96, -11.58) * mm, v(46.76, -2.86) * mm, v(63.99, -0.7) * mm]});
            skFitSpline(sketch, "E261", {"points": [v(63.99, -0.7) * mm, v(67.65, -0.24) * mm, v(75.52, -0.18) * mm, v(81.92, -0.57) * mm]});
            skFitSpline(sketch, "E262", {"points": [v(81.91, -0.69) * mm, v(91.07, -1.24) * mm, v(106.31, -1.47) * mm, v(115.77, -1.2) * mm]});
            skFitSpline(sketch, "E263", {"points": [v(115.77, -1.09) * mm, v(137.23, -0.48) * mm, v(151.56, 1.32) * mm, v(161.84, 4.7) * mm]});
            skFitSpline(sketch, "E264", {"points": [v(161.84, 4.7) * mm, v(164.4, 5.55) * mm, v(169, 7.74) * mm, v(170.07, 8.62) * mm]});
            skFitSpline(sketch, "E265", {"points": [v(170.07, 8.62) * mm, v(170.78, 9.2) * mm, v(170.75, 9.2) * mm, v(167.07, 8.29) * mm]});
            skFitSpline(sketch, "E266", {"points": [v(167.07, 8.29) * mm, v(152.9, 4.75) * mm, v(140.26, 3.12) * mm, v(124.95, 2.85) * mm]});
            skFitSpline(sketch, "E267", {"points": [v(124.95, 2.85) * mm, v(116.78, 2.7) * mm, v(111.02, 2.88) * mm, v(96.75, 3.74) * mm]});
            skFitSpline(sketch, "E268", {"points": [v(96.75, 3.74) * mm, v(76.83, 4.93) * mm, v(66.42, 4.52) * mm, v(57.25, 2.17) * mm]});
            skFitSpline(sketch, "E269", {"points": [v(57.25, 2.17) * mm, v(45.14, -0.93) * mm, v(37.4, -7.63) * mm, v(35.04, -17.03) * mm]});
            skFitSpline(sketch, "E270", {"points": [v(35.03, -17.03) * mm, v(34.42, -19.45) * mm, v(34.29, -23.8) * mm, v(34.67, -28.43) * mm]});
            skFitSpline(sketch, "E271", {"points": [v(34.67, -28.43) * mm, v(34.9, -31.2) * mm, v(34.7, -32.7) * mm, v(33.86, -34.97) * mm]});
            skFitSpline(sketch, "E272", {"points": [v(33.87, -34.97) * mm, v(33.02, -37.25) * mm, v(31.54, -39.18) * mm, v(27.95, -42.71) * mm]});
            skFitSpline(sketch, "E273", {"points": [v(27.95, -42.71) * mm, v(24.5, -46.11) * mm, v(24.05, -46.76) * mm, v(24.37, -48) * mm]});
            skFitSpline(sketch, "E274", {"points": [v(24.37, -48) * mm, v(25.15, -51.12) * mm, v(37.67, -58.5) * mm, v(48.23, -62.05) * mm]});
            skFitSpline(sketch, "E275", {"points": [v(48.23, -62.05) * mm, v(50.87, -62.93) * mm, v(51.63, -63.12) * mm, v(51.63, -62.9) * mm]});
            skFitSpline(sketch, "E276", {"points": [v(1.3, -59.45) * mm, v(4.77, -56.66) * mm, v(10.17, -51.47) * mm, v(12.74, -48.47) * mm]});
            skFitSpline(sketch, "E277", {"points": [v(12.74, -48.47) * mm, v(19.33, -40.78) * mm, v(23.86, -32.58) * mm, v(27.26, -22.18) * mm]});
            skFitSpline(sketch, "E278", {"points": [v(27.26, -22.18) * mm, v(29.31, -15.9) * mm, v(31.7, -4.9) * mm, v(31.16, -4.24) * mm]});
            skFitSpline(sketch, "E279", {"points": [v(31.16, -4.24) * mm, v(30.6, -3.56) * mm, v(27.9, -1.8) * mm, v(25.83, -0.77) * mm]});
            skFitSpline(sketch, "E280", {"points": [v(25.83, -0.77) * mm, v(20.28, 2) * mm, v(12.94, 4.03) * mm, v(4.83, 5.06) * mm]});
            skFitSpline(sketch, "E281", {"points": [v(4.83, 5.06) * mm, v(-6.8, 6.53) * mm, v(-24.36, 2.96) * mm, v(-31.37, -2.31) * mm]});
            skFitSpline(sketch, "E282", {"points": [v(-32.48, -4.39) * mm, v(-30.66, -17.46) * mm, v(-28, -26.68) * mm, v(-23.45, -35.7) * mm]});
            skFitSpline(sketch, "E283", {"points": [v(-23.45, -35.7) * mm, v(-20, -42.52) * mm, v(-15.57, -48.6) * mm, v(-9.7, -54.5) * mm]});
            skFitSpline(sketch, "E284", {"points": [v(-9.7, -54.5) * mm, v(-7.02, -57.2) * mm, v(-1.97, -61.78) * mm, v(-1.68, -61.79) * mm]});
            skFitSpline(sketch, "E285", {"points": [v(-1.68, -61.79) * mm, v(-1.63, -61.8) * mm, v(-0.28, -60.74) * mm, v(1.3, -59.45) * mm]});
            skLineSegment(sketch, "E286", {"start": v(-31.37, -2.31) * mm, "end": v(-32.64, -3.27) * mm});
            skLineSegment(sketch, "E287", {"start": v(-32.64, -3.27) * mm, "end": v(-32.48, -4.39) * mm});
            skFitSpline(sketch, "E288", {"points": [v(-51.6, -60.24) * mm, v(-43.22, -57.83) * mm, v(-31.71, -52.15) * mm, v(-28.25, -48.73) * mm]});
            skFitSpline(sketch, "E289", {"points": [v(-28.25, -48.73) * mm, v(-26.04, -46.54) * mm, v(-26.22, -45.88) * mm, v(-30.18, -41.79) * mm]});
            skFitSpline(sketch, "E290", {"points": [v(-30.18, -41.79) * mm, v(-33.45, -38.4) * mm, v(-34.46, -37.1) * mm, v(-35.42, -35) * mm]});
            skFitSpline(sketch, "E291", {"points": [v(-35.43, -35) * mm, v(-36.77, -32.07) * mm, v(-37.02, -29.38) * mm, v(-36.35, -24.93) * mm]});
            skFitSpline(sketch, "E292", {"points": [v(-36.34, -24.93) * mm, v(-34.35, -11.75) * mm, v(-41.38, -1.37) * mm, v(-55.64, 3.6) * mm]});
            skFitSpline(sketch, "E293", {"points": [v(-55.64, 3.6) * mm, v(-58.83, 4.7) * mm, v(-61.99, 5.5) * mm, v(-65.61, 6.1) * mm]});
            skFitSpline(sketch, "E294", {"points": [v(-65.61, 6.1) * mm, v(-73.72, 7.46) * mm, v(-80.66, 7.72) * mm, v(-99.2, 7.37) * mm]});
            skFitSpline(sketch, "E295", {"points": [v(-99.2, 7.45) * mm, v(-121.35, 7.04) * mm, v(-131.1, 7.5) * mm, v(-144.7, 9.59) * mm]});
            skFitSpline(sketch, "E296", {"points": [v(-144.7, 9.51) * mm, v(-151.64, 10.58) * mm, v(-161.88, 12.9) * mm, v(-168.75, 14.98) * mm]});
            skFitSpline(sketch, "E297", {"points": [v(-168.75, 14.98) * mm, v(-170.04, 15.36) * mm, v(-171.04, 15.59) * mm, v(-170.97, 15.48) * mm]});
            skFitSpline(sketch, "E298", {"points": [v(-170.97, 15.48) * mm, v(-170.9, 15.37) * mm, v(-170.1, 14.78) * mm, v(-169.18, 14.17) * mm]});
            skFitSpline(sketch, "E299", {"points": [v(-169.18, 14.17) * mm, v(-161.35, 8.97) * mm, v(-143.81, 5.17) * mm, v(-119.85, 3.5) * mm]});
            skFitSpline(sketch, "E300", {"points": [v(-119.85, 3.5) * mm, v(-110.5, 2.84) * mm, v(-106.04, 2.7) * mm, v(-87.93, 2.53) * mm]});
            skFitSpline(sketch, "E301", {"points": [v(-87.93, 2.53) * mm, v(-67.45, 2.33) * mm, v(-66.94, 2.3) * mm, v(-61.48, 1.12) * mm]});
            skFitSpline(sketch, "E302", {"points": [v(-61.48, 1.12) * mm, v(-51.63, -1.04) * mm, v(-44.64, -6.12) * mm, v(-41.6, -13.37) * mm]});
            skFitSpline(sketch, "E303", {"points": [v(-41.6, -13.37) * mm, v(-40.3, -16.46) * mm, v(-40.05, -18.06) * mm, v(-39.83, -24.6) * mm]});
            skFitSpline(sketch, "E304", {"points": [v(-39.82, -24.6) * mm, v(-39.61, -30.83) * mm, v(-39.33, -32.97) * mm, v(-38.37, -35.77) * mm]});
            skFitSpline(sketch, "E305", {"points": [v(-38.37, -35.77) * mm, v(-37.24, -39.05) * mm, v(-34.77, -42.26) * mm, v(-31.7, -44.46) * mm]});
            skFitSpline(sketch, "E306", {"points": [v(-31.32, -45.96) * mm, v(-34, -46.88) * mm, v(-38.68, -49.5) * mm, v(-44.19, -53.18) * mm]});
            skFitSpline(sketch, "E307", {"points": [v(-44.19, -53.18) * mm, v(-47.34, -55.3) * mm, v(-54.93, -60.8) * mm, v(-54.93, -60.97) * mm]});
            skFitSpline(sketch, "E308", {"points": [v(-54.93, -60.97) * mm, v(-54.93, -61.17) * mm, v(-54.48, -61.07) * mm, v(-51.6, -60.24) * mm]});
            skLineSegment(sketch, "E309", {"start": v(-31.7, -44.46) * mm, "end": v(-30.15, -45.56) * mm});
            skLineSegment(sketch, "E310", {"start": v(-30.15, -45.56) * mm, "end": v(-31.32, -45.96) * mm});
            skLineSegment(sketch, "E311", {"start": v(-31.32, -45.96) * mm, "end": v(-31.7, -44.46) * mm});
            skFitSpline(sketch, "E312", {"points": [v(73.7, -60.57) * mm, v(72.68, -59.73) * mm, v(69.47, -58.32) * mm, v(64.47, -56.51) * mm]});
            skFitSpline(sketch, "E313", {"points": [v(64.47, -56.51) * mm, v(55.45, -53.26) * mm, v(51.29, -51.36) * mm, v(47.28, -48.69) * mm]});
            skFitSpline(sketch, "E314", {"points": [v(47.28, -48.69) * mm, v(45.83, -47.72) * mm, v(44.74, -47.15) * mm, v(44.31, -47.15) * mm]});
            skFitSpline(sketch, "E315", {"points": [v(44.31, -47.15) * mm, v(42.84, -47.15) * mm, v(38.66, -46.35) * mm, v(36.6, -45.67) * mm]});
            skFitSpline(sketch, "E316", {"points": [v(33.3, -47.1) * mm, v(34.77, -48.36) * mm, v(39.3, -51.32) * mm, v(41.79, -52.64) * mm]});
            skFitSpline(sketch, "E317", {"points": [v(41.79, -52.64) * mm, v(50.7, -57.36) * mm, v(63.38, -60.78) * mm, v(72.87, -61.03) * mm]});
            skLineSegment(sketch, "E318", {"start": v(36.6, -45.67) * mm, "end": v(34.4, -44.95) * mm});
            skLineSegment(sketch, "E319", {"start": v(34.4, -44.95) * mm, "end": v(33.38, -45.62) * mm});
            skLineSegment(sketch, "E320", {"start": v(33.38, -45.62) * mm, "end": v(32.37, -46.3) * mm});
            skLineSegment(sketch, "E321", {"start": v(32.37, -46.3) * mm, "end": v(33.3, -47.1) * mm});
            skFitSpline(sketch, "E322", {"points": [v(-66.93, -57.6) * mm, v(-55.21, -55.9) * mm, v(-44.01, -51.72) * mm, v(-36.51, -46.24) * mm]});
            skFitSpline(sketch, "E323", {"points": [v(-36.51, -46.24) * mm, v(-35.69, -45.63) * mm, v(-35.02, -45.08) * mm, v(-35.02, -45) * mm]});
            skFitSpline(sketch, "E324", {"points": [v(-35.02, -45) * mm, v(-35.03, -44.93) * mm, v(-35.46, -44.57) * mm, v(-36, -44.2) * mm]});
            skLineSegment(sketch, "E325", {"start": v(72.87, -61.03) * mm, "end": v(74.3, -61.06) * mm});
            skLineSegment(sketch, "E326", {"start": v(74.3, -61.06) * mm, "end": v(73.7, -60.57) * mm});
            skLineSegment(sketch, "E327", {"start": v(73.7, -60.57) * mm, "end": v(73.7, -60.57) * mm});
            skLineSegment(sketch, "E328", {"start": v(73.7, -60.57) * mm, "end": v(72.87, -61.03) * mm});
            skFitSpline(sketch, "E329", {"points": [v(-38.4, -44.03) * mm, v(-40.36, -44.66) * mm, v(-43.06, -45.16) * mm, v(-45.7, -45.37) * mm]});
            skFitSpline(sketch, "E330", {"points": [v(-45.7, -45.37) * mm, v(-47.7, -45.52) * mm, v(-47.97, -45.6) * mm, v(-49.41, -46.56) * mm]});
            skFitSpline(sketch, "E331", {"points": [v(-49.41, -46.56) * mm, v(-53.18, -49.02) * mm, v(-57.36, -50.76) * mm, v(-67.17, -53.96) * mm]});
            skFitSpline(sketch, "E332", {"points": [v(-67.17, -53.96) * mm, v(-73.7, -56.1) * mm, v(-75.62, -56.85) * mm, v(-76.73, -57.74) * mm]});
            skLineSegment(sketch, "E333", {"start": v(-36, -44.2) * mm, "end": v(-36.95, -43.55) * mm});
            skLineSegment(sketch, "E334", {"start": v(-36.95, -43.55) * mm, "end": v(-38.4, -44.03) * mm});
            skFitSpline(sketch, "E335", {"points": [v(-73.41, -58.1) * mm, v(-71.24, -58.03) * mm, v(-68.32, -57.8) * mm, v(-66.93, -57.6) * mm]});
            skLineSegment(sketch, "E336", {"start": v(-76.73, -57.74) * mm, "end": v(-77.37, -58.26) * mm});
            skLineSegment(sketch, "E337", {"start": v(-77.37, -58.26) * mm, "end": v(-73.41, -58.1) * mm});
            skFitSpline(sketch, "E338", {"points": [v(90.23, -54.91) * mm, v(89.44, -53.94) * mm, v(84.75, -52.27) * mm, v(78.99, -50.9) * mm]});
            skFitSpline(sketch, "E339", {"points": [v(78.99, -50.9) * mm, v(77.6, -50.57) * mm, v(75.06, -49.97) * mm, v(73.35, -49.56) * mm]});
            skFitSpline(sketch, "E340", {"points": [v(73.35, -49.56) * mm, v(69.47, -48.64) * mm, v(66.43, -47.72) * mm, v(65.23, -47.11) * mm]});
            skFitSpline(sketch, "E341", {"points": [v(65.23, -47.11) * mm, v(64.34, -46.66) * mm, v(64.2, -46.66) * mm, v(60.73, -47.02) * mm]});
            skFitSpline(sketch, "E342", {"points": [v(60.73, -47.02) * mm, v(58.75, -47.22) * mm, v(56.3, -47.4) * mm, v(55.28, -47.42) * mm]});
            skFitSpline(sketch, "E343", {"points": [v(55.28, -47.42) * mm, v(54.26, -47.43) * mm, v(53.16, -47.51) * mm, v(52.84, -47.6) * mm]});
            skFitSpline(sketch, "E344", {"points": [v(52.84, -47.6) * mm, v(52.26, -47.76) * mm, v(52.27, -47.77) * mm, v(53.2, -48.54) * mm]});
            skFitSpline(sketch, "E345", {"points": [v(53.2, -48.54) * mm, v(56.22, -51.03) * mm, v(63.82, -53.34) * mm, v(72.75, -54.47) * mm]});
            skFitSpline(sketch, "E346", {"points": [v(72.75, -54.47) * mm, v(77.41, -55.06) * mm, v(80.38, -55.24) * mm, v(85.67, -55.28) * mm]});
            skFitSpline(sketch, "E347", {"points": [v(85.67, -55.28) * mm, v(90.22, -55.31) * mm, v(90.54, -55.28) * mm, v(90.23, -54.91) * mm]});
            skFitSpline(sketch, "E348", {"points": [v(-79.77, -51.95) * mm, v(-72.42, -51.54) * mm, v(-66.1, -50.57) * mm, v(-61.62, -49.17) * mm]});
            skFitSpline(sketch, "E349", {"points": [v(-61.62, -49.17) * mm, v(-59.5, -48.5) * mm, v(-56.46, -47.02) * mm, v(-55.35, -46.1) * mm]});
            skFitSpline(sketch, "E350", {"points": [v(-58.23, -45.26) * mm, v(-60.18, -45.1) * mm, v(-62.93, -44.77) * mm, v(-64.34, -44.54) * mm]});
            skFitSpline(sketch, "E351", {"points": [v(-64.34, -44.54) * mm, v(-66.48, -44.2) * mm, v(-67, -44.18) * mm, v(-67.46, -44.43) * mm]});
            skFitSpline(sketch, "E352", {"points": [v(-67.46, -44.43) * mm, v(-68.61, -45.08) * mm, v(-71.36, -45.78) * mm, v(-78.21, -47.17) * mm]});
            skFitSpline(sketch, "E353", {"points": [v(-78.21, -47.17) * mm, v(-86.27, -48.8) * mm, v(-90.02, -49.77) * mm, v(-91.88, -50.7) * mm]});
            skFitSpline(sketch, "E354", {"points": [v(-91.88, -50.7) * mm, v(-93.84, -51.68) * mm, v(-93.72, -51.92) * mm, v(-91.25, -52.01) * mm]});
            skFitSpline(sketch, "E355", {"points": [v(-91.25, -52.01) * mm, v(-86.62, -52.19) * mm, v(-83.9, -52.17) * mm, v(-79.77, -51.95) * mm]});
            skLineSegment(sketch, "E356", {"start": v(-55.35, -46.1) * mm, "end": v(-54.68, -45.56) * mm});
            skLineSegment(sketch, "E357", {"start": v(-54.68, -45.56) * mm, "end": v(-58.23, -45.26) * mm});
            skFitSpline(sketch, "E358", {"points": [v(106.59, -48.24) * mm, v(109.85, -47.9) * mm, v(113.06, -47.31) * mm, v(113.7, -46.96) * mm]});
            skFitSpline(sketch, "E359", {"points": [v(113.7, -46.96) * mm, v(113.9, -46.84) * mm, v(112.74, -46.64) * mm, v(110.85, -46.47) * mm]});
            skFitSpline(sketch, "E360", {"points": [v(110.85, -46.47) * mm, v(103.26, -45.77) * mm, v(88.46, -43.28) * mm, v(85, -42.12) * mm]});
            skLineSegment(sketch, "E361", {"start": v(-79.77, -51.95) * mm, "end": v(-79.77, -51.95) * mm});
            skFitSpline(sketch, "E362", {"points": [v(80, -42.82) * mm, v(78.05, -43.48) * mm, v(75.22, -44.34) * mm, v(73.7, -44.73) * mm]});
            skFitSpline(sketch, "E363", {"points": [v(73.7, -44.73) * mm, v(72.19, -45.12) * mm, v(71.1, -45.5) * mm, v(71.3, -45.58) * mm]});
            skFitSpline(sketch, "E364", {"points": [v(71.3, -45.58) * mm, v(73.25, -46.33) * mm, v(82.82, -47.92) * mm, v(87.75, -48.31) * mm]});
            skFitSpline(sketch, "E365", {"points": [v(87.75, -48.31) * mm, v(92.16, -48.67) * mm, v(102.98, -48.63) * mm, v(106.59, -48.24) * mm]});
            skLineSegment(sketch, "E366", {"start": v(85, -42.12) * mm, "end": v(83.52, -41.62) * mm});
            skLineSegment(sketch, "E367", {"start": v(83.52, -41.62) * mm, "end": v(80, -42.82) * mm});
            skFitSpline(sketch, "E368", {"points": [v(56.57, -45.23) * mm, v(60.2, -44.95) * mm, v(64.12, -44.26) * mm, v(66.99, -43.4) * mm]});
            skFitSpline(sketch, "E369", {"points": [v(66.99, -43.4) * mm, v(68.94, -42.81) * mm, v(72.86, -41.07) * mm, v(73.1, -40.67) * mm]});
            skFitSpline(sketch, "E370", {"points": [v(73.1, -40.67) * mm, v(73.26, -40.41) * mm, v(69.06, -39.09) * mm, v(66.26, -38.5) * mm]});
            skFitSpline(sketch, "E371", {"points": [v(66.26, -38.5) * mm, v(62.58, -37.75) * mm, v(60.52, -37.86) * mm, v(57.2, -38.98) * mm]});
            skFitSpline(sketch, "E372", {"points": [v(57.2, -38.98) * mm, v(51.53, -40.9) * mm, v(45.52, -41.59) * mm, v(41.16, -40.83) * mm]});
            skFitSpline(sketch, "E373", {"points": [v(41.16, -40.83) * mm, v(39.96, -40.62) * mm, v(38.83, -40.4) * mm, v(38.64, -40.33) * mm]});
            skFitSpline(sketch, "E374", {"points": [v(38.64, -40.33) * mm, v(38.16, -40.16) * mm, v(36.36, -42.84) * mm, v(36.79, -43.1) * mm]});
            skFitSpline(sketch, "E375", {"points": [v(36.79, -43.1) * mm, v(37.29, -43.4) * mm, v(40.66, -44.27) * mm, v(42.92, -44.66) * mm]});
            skFitSpline(sketch, "E376", {"points": [v(42.92, -44.66) * mm, v(47.23, -45.41) * mm, v(51.8, -45.6) * mm, v(56.57, -45.23) * mm]});
            skFitSpline(sketch, "E377", {"points": [v(-83.25, -44.4) * mm, v(-79.89, -44) * mm, v(-74.56, -43.12) * mm, v(-73.84, -42.86) * mm]});
            skFitSpline(sketch, "E378", {"points": [v(-73.84, -42.86) * mm, v(-73.57, -42.76) * mm, v(-74.51, -42.38) * mm, v(-76.43, -41.8) * mm]});
            skFitSpline(sketch, "E379", {"points": [v(-76.43, -41.8) * mm, v(-78.09, -41.32) * mm, v(-80.88, -40.34) * mm, v(-82.65, -39.64) * mm]});
            skFitSpline(sketch, "E380", {"points": [v(-82.65, -39.64) * mm, v(-85.14, -38.65) * mm, v(-85.98, -38.42) * mm, v(-86.42, -38.58) * mm]});
            skFitSpline(sketch, "E381", {"points": [v(-86.42, -38.58) * mm, v(-89.26, -39.66) * mm, v(-102.55, -41.5) * mm, v(-112.35, -42.16) * mm]});
            skFitSpline(sketch, "E382", {"points": [v(-112.35, -42.16) * mm, v(-114.7, -42.32) * mm, v(-116.48, -42.53) * mm, v(-116.31, -42.62) * mm]});
            skFitSpline(sketch, "E383", {"points": [v(-116.31, -42.62) * mm, v(-115.16, -43.24) * mm, v(-109.02, -44.33) * mm, v(-104.37, -44.74) * mm]});
            skFitSpline(sketch, "E384", {"points": [v(-104.37, -44.74) * mm, v(-100.47, -45.08) * mm, v(-87.07, -44.87) * mm, v(-83.25, -44.4) * mm]});
            skFitSpline(sketch, "E385", {"points": [v(-46.05, -43.05) * mm, v(-43.88, -42.81) * mm, v(-39.77, -41.99) * mm, v(-39.17, -41.66) * mm]});
            skFitSpline(sketch, "E386", {"points": [v(-39.17, -41.66) * mm, v(-38.98, -41.56) * mm, v(-39.17, -41.07) * mm, v(-39.76, -40.12) * mm]});
            skFitSpline(sketch, "E387", {"points": [v(-39.76, -40.12) * mm, v(-40.5, -38.9) * mm, v(-40.7, -38.74) * mm, v(-41.2, -38.87) * mm]});
            skFitSpline(sketch, "E388", {"points": [v(-41.2, -38.87) * mm, v(-46.08, -40.1) * mm, v(-53.4, -39.2) * mm, v(-60.06, -36.57) * mm]});
            skFitSpline(sketch, "E389", {"points": [v(-60.06, -36.57) * mm, v(-62.15, -35.74) * mm, v(-62.66, -35.63) * mm, v(-64.45, -35.63) * mm]});
            skFitSpline(sketch, "E390", {"points": [v(-64.45, -35.63) * mm, v(-65.57, -35.63) * mm, v(-67.26, -35.75) * mm, v(-68.2, -35.89) * mm]});
            skFitSpline(sketch, "E391", {"points": [v(-68.2, -35.89) * mm, v(-70.39, -36.2) * mm, v(-75.33, -37.54) * mm, v(-75.33, -37.8) * mm]});
            skFitSpline(sketch, "E392", {"points": [v(-75.33, -37.8) * mm, v(-75.33, -37.92) * mm, v(-74.62, -38.4) * mm, v(-73.75, -38.9) * mm]});
            skFitSpline(sketch, "E393", {"points": [v(-73.75, -38.9) * mm, v(-67.27, -42.52) * mm, v(-56.32, -44.16) * mm, v(-46.05, -43.05) * mm]});
            skFitSpline(sketch, "E394", {"points": [v(105.99, -42.1) * mm, v(114.97, -41.64) * mm, v(122.53, -40.24) * mm, v(128.8, -37.9) * mm]});
            skFitSpline(sketch, "E395", {"points": [v(128.8, -37.9) * mm, v(131.33, -36.96) * mm, v(134.47, -35.45) * mm, v(135.27, -34.8) * mm]});
            skFitSpline(sketch, "E396", {"points": [v(135.27, -34.8) * mm, v(135.75, -34.4) * mm, v(135.75, -34.4) * mm, v(135.27, -34.53) * mm]});
            skFitSpline(sketch, "E397", {"points": [v(135.27, -34.53) * mm, v(134.23, -34.8) * mm, v(130.34, -35.37) * mm, v(127.95, -35.62) * mm]});
            skFitSpline(sketch, "E398", {"points": [v(127.95, -35.62) * mm, v(122.8, -36.16) * mm, v(118.52, -36.35) * mm, v(111.63, -36.35) * mm]});
            skFitSpline(sketch, "E399", {"points": [v(111.63, -36.35) * mm, v(104.53, -36.35) * mm, v(100.49, -36.11) * mm, v(97.35, -35.52) * mm]});
            skFitSpline(sketch, "E400", {"points": [v(94.1, -36.18) * mm, v(93.25, -36.72) * mm, v(91.16, -37.88) * mm, v(89.46, -38.77) * mm]});
            skFitSpline(sketch, "E401", {"points": [v(89.46, -38.77) * mm, v(87.76, -39.65) * mm, v(86.47, -40.43) * mm, v(86.58, -40.5) * mm]});
            skFitSpline(sketch, "E402", {"points": [v(86.58, -40.5) * mm, v(87.37, -40.99) * mm, v(93.48, -41.89) * mm, v(97.47, -42.1) * mm]});
            skFitSpline(sketch, "E403", {"points": [v(97.47, -42.1) * mm, v(99.25, -42.2) * mm, v(100.87, -42.3) * mm, v(101.07, -42.31) * mm]});
            skFitSpline(sketch, "E404", {"points": [v(101.07, -42.31) * mm, v(101.26, -42.33) * mm, v(103.48, -42.24) * mm, v(105.99, -42.1) * mm]});
            skLineSegment(sketch, "E405", {"start": v(97.35, -35.52) * mm, "end": v(95.67, -35.2) * mm});
            skLineSegment(sketch, "E406", {"start": v(95.67, -35.2) * mm, "end": v(94.1, -36.18) * mm});
            skFitSpline(sketch, "E407", {"points": [v(-93.81, -38) * mm, v(-90.97, -37.68) * mm, v(-88.77, -37.3) * mm, v(-88.78, -37.1) * mm]});
            skFitSpline(sketch, "E408", {"points": [v(-88.78, -37.1) * mm, v(-88.78, -37.02) * mm, v(-89.78, -36.41) * mm, v(-90.99, -35.75) * mm]});
            skFitSpline(sketch, "E409", {"points": [v(-90.99, -35.75) * mm, v(-92.2, -35.1) * mm, v(-94.21, -33.88) * mm, v(-95.46, -33.06) * mm]});
            skFitSpline(sketch, "E410", {"points": [v(-99.44, -31.86) * mm, v(-102.1, -32.32) * mm, v(-116.41, -32.22) * mm, v(-121.77, -31.7) * mm]});
            skFitSpline(sketch, "E411", {"points": [v(-121.77, -31.7) * mm, v(-127.16, -31.19) * mm, v(-132.4, -30.47) * mm, v(-135.2, -29.86) * mm]});
            skFitSpline(sketch, "E412", {"points": [v(-135.2, -29.86) * mm, v(-136.37, -29.6) * mm, v(-137.38, -29.44) * mm, v(-137.43, -29.48) * mm]});
            skFitSpline(sketch, "E413", {"points": [v(-137.43, -29.48) * mm, v(-137.6, -29.65) * mm, v(-135.2, -31.05) * mm, v(-132.93, -32.12) * mm]});
            skFitSpline(sketch, "E414", {"points": [v(-132.93, -32.12) * mm, v(-122.81, -36.9) * mm, v(-106.16, -39.4) * mm, v(-93.81, -38) * mm]});
            skLineSegment(sketch, "E415", {"start": v(-95.46, -33.06) * mm, "end": v(-97.74, -31.56) * mm});
            skLineSegment(sketch, "E416", {"start": v(-97.74, -31.56) * mm, "end": v(-99.44, -31.86) * mm});
            skFitSpline(sketch, "E417", {"points": [v(48.75, -38) * mm, v(50.9, -37.72) * mm, v(54.1, -36.82) * mm, v(54.84, -36.28) * mm]});
            skFitSpline(sketch, "E418", {"points": [v(54.84, -36.28) * mm, v(55.24, -35.99) * mm, v(55.05, -35.86) * mm, v(52.85, -34.95) * mm]});
            skFitSpline(sketch, "E419", {"points": [v(52.85, -34.95) * mm, v(48.2, -33.02) * mm, v(43.06, -31.53) * mm, v(42.19, -31.86) * mm]});
            skFitSpline(sketch, "E420", {"points": [v(42.19, -31.86) * mm, v(42, -31.94) * mm, v(41.78, -32.28) * mm, v(41.69, -32.62) * mm]});
            skFitSpline(sketch, "E421", {"points": [v(41.69, -32.62) * mm, v(41.6, -32.97) * mm, v(41.1, -34.28) * mm, v(40.55, -35.53) * mm]});
            skFitSpline(sketch, "E422", {"points": [v(40.55, -35.53) * mm, v(40.01, -36.8) * mm, v(39.65, -37.9) * mm, v(39.74, -37.98) * mm]});
            skFitSpline(sketch, "E423", {"points": [v(39.74, -37.98) * mm, v(40.25, -38.5) * mm, v(44.74, -38.5) * mm, v(48.75, -38) * mm]});
            skFitSpline(sketch, "E424", {"points": [v(-41.8, -36.5) * mm, v(-41.77, -36.46) * mm, v(-42, -35.8) * mm, v(-42.3, -35.01) * mm]});
            skFitSpline(sketch, "E425", {"points": [v(-42.3, -35.01) * mm, v(-42.62, -34.23) * mm, v(-43.13, -32.8) * mm, v(-43.43, -31.85) * mm]});
            skFitSpline(sketch, "E426", {"points": [v(-43.43, -31.85) * mm, v(-44.07, -29.85) * mm, v(-44, -29.88) * mm, v(-46.92, -30.49) * mm]});
            skFitSpline(sketch, "E427", {"points": [v(-46.92, -30.49) * mm, v(-49.9, -31.1) * mm, v(-57.33, -33.57) * mm, v(-57.33, -33.95) * mm]});
            skFitSpline(sketch, "E428", {"points": [v(-57.33, -33.95) * mm, v(-57.33, -34.6) * mm, v(-51.5, -36.25) * mm, v(-47.99, -36.58) * mm]});
            skFitSpline(sketch, "E429", {"points": [v(-47.99, -36.58) * mm, v(-46.02, -36.76) * mm, v(-42.02, -36.72) * mm, v(-41.8, -36.5) * mm]});
            skFitSpline(sketch, "E430", {"points": [v(85.68, -35.64) * mm, v(90.93, -34.94) * mm, v(95.79, -33.7) * mm, v(95.79, -33.04) * mm]});
            skFitSpline(sketch, "E431", {"points": [v(95.79, -33.04) * mm, v(95.79, -32.72) * mm, v(88, -29.73) * mm, v(85.03, -28.91) * mm]});
            skFitSpline(sketch, "E432", {"points": [v(85.03, -28.91) * mm, v(81.57, -27.95) * mm, v(78.72, -27.49) * mm, v(75.23, -27.31) * mm]});
            skFitSpline(sketch, "E433", {"points": [v(69.96, -28.56) * mm, v(67.13, -30.25) * mm, v(63.48, -31.92) * mm, v(61.8, -32.3) * mm]});
            skFitSpline(sketch, "E434", {"points": [v(61.8, -32.3) * mm, v(60.7, -32.55) * mm, v(60.52, -32.67) * mm, v(60.08, -33.6) * mm]});
            skLineSegment(sketch, "E435", {"start": v(75.23, -27.31) * mm, "end": v(72.3, -27.16) * mm});
            skLineSegment(sketch, "E436", {"start": v(72.3, -27.16) * mm, "end": v(69.96, -28.56) * mm});
            skFitSpline(sketch, "E437", {"points": [v(60.11, -34.86) * mm, v(60.95, -35.23) * mm, v(64.02, -35.86) * mm, v(66.27, -36.1) * mm]});
            skFitSpline(sketch, "E438", {"points": [v(66.27, -36.1) * mm, v(69.89, -36.5) * mm, v(81.23, -36.22) * mm, v(85.68, -35.64) * mm]});
            skLineSegment(sketch, "E439", {"start": v(60.08, -33.6) * mm, "end": v(59.58, -34.61) * mm});
            skLineSegment(sketch, "E440", {"start": v(59.58, -34.61) * mm, "end": v(60.11, -34.86) * mm});
            skFitSpline(sketch, "E441", {"points": [v(-67.83, -33.47) * mm, v(-66.28, -33.34) * mm, v(-64.26, -33.07) * mm, v(-63.34, -32.86) * mm]});
            skFitSpline(sketch, "E442", {"points": [v(-62.09, -31.4) * mm, v(-62.48, -30.36) * mm, v(-62.55, -30.31) * mm, v(-64.44, -29.66) * mm]});
            skFitSpline(sketch, "E443", {"points": [v(-64.44, -29.66) * mm, v(-66.58, -28.92) * mm, v(-69.7, -27.31) * mm, v(-72.2, -25.65) * mm]});
            skFitSpline(sketch, "E444", {"points": [v(-72.2, -25.65) * mm, v(-73.66, -24.68) * mm, v(-73.96, -24.57) * mm, v(-75.7, -24.44) * mm]});
            skFitSpline(sketch, "E445", {"points": [v(-75.7, -24.44) * mm, v(-79.03, -24.2) * mm, v(-84.99, -25) * mm, v(-89.34, -26.3) * mm]});
            skFitSpline(sketch, "E446", {"points": [v(-89.34, -26.3) * mm, v(-92.34, -27.19) * mm, v(-97.9, -29.2) * mm, v(-97.9, -29.39) * mm]});
            skFitSpline(sketch, "E447", {"points": [v(-97.9, -29.39) * mm, v(-97.9, -29.5) * mm, v(-97.38, -29.8) * mm, v(-96.75, -30.06) * mm]});
            skFitSpline(sketch, "E448", {"points": [v(-96.75, -30.06) * mm, v(-91, -32.51) * mm, v(-76.66, -34.2) * mm, v(-67.83, -33.47) * mm]});
            skLineSegment(sketch, "E449", {"start": v(-63.34, -32.86) * mm, "end": v(-61.68, -32.48) * mm});
            skLineSegment(sketch, "E450", {"start": v(-61.68, -32.48) * mm, "end": v(-62.09, -31.4) * mm});
            skFitSpline(sketch, "E451", {"points": [v(118.83, -31.68) * mm, v(130.49, -30.44) * mm, v(142.66, -27.2) * mm, v(151.53, -22.97) * mm]});
            skFitSpline(sketch, "E452", {"points": [v(151.53, -22.97) * mm, v(153.34, -22.1) * mm, v(154.8, -21.37) * mm, v(154.77, -21.34) * mm]});
            skFitSpline(sketch, "E453", {"points": [v(154.77, -21.34) * mm, v(154.73, -21.3) * mm, v(153.68, -21.48) * mm, v(152.43, -21.72) * mm]});
            skFitSpline(sketch, "E454", {"points": [v(152.43, -21.72) * mm, v(146.91, -22.78) * mm, v(141.94, -23.1) * mm, v(121.95, -23.64) * mm]});
            skFitSpline(sketch, "E455", {"points": [v(121.95, -23.64) * mm, v(111.54, -23.92) * mm, v(109.52, -24.12) * mm, v(107.17, -25.08) * mm]});
            skFitSpline(sketch, "E456", {"points": [v(107.17, -25.08) * mm, v(104.75, -26.06) * mm, v(99.52, -27.56) * mm, v(96.18, -28.2) * mm]});
            skFitSpline(sketch, "E457", {"points": [v(94.58, -29.32) * mm, v(97.26, -30.5) * mm, v(100.79, -31.38) * mm, v(104.79, -31.87) * mm]});
            skFitSpline(sketch, "E458", {"points": [v(104.79, -31.87) * mm, v(106.77, -32.12) * mm, v(115.92, -32) * mm, v(118.83, -31.68) * mm]});
            skLineSegment(sketch, "E459", {"start": v(96.18, -28.2) * mm, "end": v(93.33, -28.76) * mm});
            skLineSegment(sketch, "E460", {"start": v(93.33, -28.76) * mm, "end": v(94.58, -29.32) * mm});
            skFitSpline(sketch, "E461", {"points": [v(55.9, -29.85) * mm, v(61.53, -29.44) * mm, v(66.06, -28.38) * mm, v(67.1, -27.23) * mm]});
            skFitSpline(sketch, "E462", {"points": [v(67.1, -27.23) * mm, v(67.59, -26.7) * mm, v(67.74, -26.8) * mm, v(65.19, -26.04) * mm]});
            skFitSpline(sketch, "E463", {"points": [v(65.19, -26.04) * mm, v(62.78, -25.34) * mm, v(58.21, -24.43) * mm, v(54.87, -24) * mm]});
            skFitSpline(sketch, "E464", {"points": [v(54.87, -24) * mm, v(51.61, -23.57) * mm, v(46.06, -23.47) * mm, v(45.13, -23.83) * mm]});
            skFitSpline(sketch, "E465", {"points": [v(45.13, -23.83) * mm, v(44.6, -24.03) * mm, v(44.4, -24.47) * mm, v(43.63, -26.93) * mm]});
            skFitSpline(sketch, "E466", {"points": [v(43.63, -26.93) * mm, v(43.14, -28.51) * mm, v(42.75, -29.87) * mm, v(42.75, -29.96) * mm]});
            skFitSpline(sketch, "E467", {"points": [v(42.75, -29.96) * mm, v(42.75, -30.2) * mm, v(52.07, -30.13) * mm, v(55.9, -29.85) * mm]});
            skFitSpline(sketch, "E468", {"points": [v(-44.63, -28.25) * mm, v(-44.63, -28.15) * mm, v(-45, -26.8) * mm, v(-45.43, -25.22) * mm]});
            skFitSpline(sketch, "E469", {"points": [v(-45.43, -25.22) * mm, v(-45.98, -23.25) * mm, v(-46.36, -22.3) * mm, v(-46.68, -22.1) * mm]});
            skFitSpline(sketch, "E470", {"points": [v(-46.68, -22.1) * mm, v(-47.45, -21.65) * mm, v(-56.94, -21.77) * mm, v(-60.21, -22.28) * mm]});
            skFitSpline(sketch, "E471", {"points": [v(-60.21, -22.28) * mm, v(-63.2, -22.74) * mm, v(-67.91, -23.71) * mm, v(-68.82, -24.05) * mm]});
            skFitSpline(sketch, "E472", {"points": [v(-68.63, -24.9) * mm, v(-67.03, -26.25) * mm, v(-61.54, -27.47) * mm, v(-54.93, -27.94) * mm]});
            skFitSpline(sketch, "E473", {"points": [v(-54.93, -27.94) * mm, v(-48.85, -28.38) * mm, v(-44.6, -28.5) * mm, v(-44.63, -28.25) * mm]});
            skLineSegment(sketch, "E474", {"start": v(-68.82, -24.05) * mm, "end": v(-69.39, -24.26) * mm});
            skLineSegment(sketch, "E475", {"start": v(-69.39, -24.26) * mm, "end": v(-68.63, -24.9) * mm});
            skFitSpline(sketch, "E476", {"points": [v(-101.9, -27.24) * mm, v(-100.46, -26.96) * mm, v(-98.36, -26.4) * mm, v(-97.24, -25.98) * mm]});
            skFitSpline(sketch, "E477", {"points": [v(-98.76, -24.34) * mm, v(-102.57, -23.37) * mm, v(-106.41, -22.1) * mm, v(-108.89, -20.98) * mm]});
            skFitSpline(sketch, "E478", {"points": [v(-108.89, -20.98) * mm, v(-109.72, -20.6) * mm, v(-111.02, -20.18) * mm, v(-111.77, -20.05) * mm]});
            skFitSpline(sketch, "E479", {"points": [v(-111.77, -20.05) * mm, v(-114.27, -19.6) * mm, v(-120.26, -19.09) * mm, v(-127.3, -18.71) * mm]});
            skFitSpline(sketch, "E480", {"points": [v(-127.3, -18.71) * mm, v(-135.85, -18.25) * mm, v(-142.42, -17.75) * mm, v(-146.37, -17.25) * mm]});
            skFitSpline(sketch, "E481", {"points": [v(-146.37, -17.25) * mm, v(-149.14, -16.9) * mm, v(-154.56, -15.92) * mm, v(-155.64, -15.58) * mm]});
            skFitSpline(sketch, "E482", {"points": [v(-155.64, -15.58) * mm, v(-156.63, -15.26) * mm, v(-155.13, -16.21) * mm, v(-152.62, -17.5) * mm]});
            skFitSpline(sketch, "E483", {"points": [v(-152.62, -17.5) * mm, v(-143.22, -22.3) * mm, v(-127.87, -26.64) * mm, v(-116.5, -27.7) * mm]});
            skFitSpline(sketch, "E484", {"points": [v(-116.5, -27.7) * mm, v(-112.45, -28.07) * mm, v(-104.9, -27.84) * mm, v(-101.9, -27.24) * mm]});
            skLineSegment(sketch, "E485", {"start": v(-97.24, -25.98) * mm, "end": v(-95.19, -25.24) * mm});
            skLineSegment(sketch, "E486", {"start": v(-95.19, -25.24) * mm, "end": v(-98.76, -24.34) * mm});
            skFitSpline(sketch, "E487", {"points": [v(90.63, -24.83) * mm, v(97.5, -24.26) * mm, v(103.06, -23.01) * mm, v(105.3, -21.55) * mm]});
            skFitSpline(sketch, "E488", {"points": [v(105.3, -21.55) * mm, v(106.1, -21.03) * mm, v(105.86, -20.9) * mm, v(102.85, -20.3) * mm]});
            skFitSpline(sketch, "E489", {"points": [v(102.85, -20.3) * mm, v(98.21, -19.36) * mm, v(88.43, -18.6) * mm, v(81.1, -18.6) * mm]});
            skFitSpline(sketch, "E490", {"points": [v(81.1, -18.6) * mm, v(77.85, -18.6) * mm, v(77.16, -18.66) * mm, v(76.4, -19.04) * mm]});
            skFitSpline(sketch, "E491", {"points": [v(76.4, -19.04) * mm, v(74.86, -19.82) * mm, v(72, -20.78) * mm, v(69.55, -21.33) * mm]});
            skFitSpline(sketch, "E492", {"points": [v(68.59, -22.6) * mm, v(70.68, -23.72) * mm, v(74.22, -24.52) * mm, v(78.87, -24.91) * mm]});
            skFitSpline(sketch, "E493", {"points": [v(78.87, -24.91) * mm, v(81.08, -25.1) * mm, v(87.95, -25.05) * mm, v(90.63, -24.83) * mm]});
            skLineSegment(sketch, "E494", {"start": v(69.55, -21.33) * mm, "end": v(67.19, -21.87) * mm});
            skLineSegment(sketch, "E495", {"start": v(67.19, -21.87) * mm, "end": v(68.59, -22.6) * mm});
            skFitSpline(sketch, "E496", {"points": [v(-74.97, -21.36) * mm, v(-72, -20.83) * mm, v(-69.1, -19.82) * mm, v(-69.1, -19.3) * mm]});
            skFitSpline(sketch, "E497", {"points": [v(-69.1, -19.3) * mm, v(-69.1, -19.2) * mm, v(-69.55, -19.04) * mm, v(-70.11, -18.94) * mm]});
            skFitSpline(sketch, "E498", {"points": [v(-70.11, -18.94) * mm, v(-71.6, -18.7) * mm, v(-75.67, -17.24) * mm, v(-77.36, -16.35) * mm]});
            skFitSpline(sketch, "E499", {"points": [v(-88.65, -15.6) * mm, v(-98.65, -15.62) * mm, v(-103.16, -15.9) * mm, v(-106.41, -16.76) * mm]});
            skLineSegment(sketch, "E500", {"start": v(-77.36, -16.35) * mm, "end": v(-78.81, -15.6) * mm});
            skLineSegment(sketch, "E501", {"start": v(-78.81, -15.6) * mm, "end": v(-88.65, -15.6) * mm});
            skFitSpline(sketch, "E502", {"points": [v(-106.3, -17.83) * mm, v(-103, -19.74) * mm, v(-97.1, -21) * mm, v(-87.57, -21.8) * mm]});
            skFitSpline(sketch, "E503", {"points": [v(-87.57, -21.8) * mm, v(-85.12, -22.02) * mm, v(-77.05, -21.74) * mm, v(-74.97, -21.36) * mm]});
            skLineSegment(sketch, "E504", {"start": v(-106.41, -16.76) * mm, "end": v(-107.61, -17.07) * mm});
            skLineSegment(sketch, "E505", {"start": v(-107.61, -17.07) * mm, "end": v(-106.3, -17.83) * mm});
            skFitSpline(sketch, "E506", {"points": [v(58.59, -20.6) * mm, v(62.7, -20.18) * mm, v(66.37, -19.5) * mm, v(68.88, -18.7) * mm]});
            skFitSpline(sketch, "E507", {"points": [v(68.88, -18.7) * mm, v(70.96, -18.04) * mm, v(72.43, -17.22) * mm, v(72.12, -16.9) * mm]});
            skFitSpline(sketch, "E508", {"points": [v(72.12, -16.9) * mm, v(72, -16.8) * mm, v(70.6, -16.32) * mm, v(69, -15.86) * mm]});
            skFitSpline(sketch, "E509", {"points": [v(69, -15.86) * mm, v(62.87, -14.1) * mm, v(56.72, -13.3) * mm, v(52.93, -13.76) * mm]});
            skFitSpline(sketch, "E510", {"points": [v(52.93, -13.76) * mm, v(50.01, -14.12) * mm, v(49.64, -14.28) * mm, v(48.64, -15.64) * mm]});
            skFitSpline(sketch, "E511", {"points": [v(48.64, -15.64) * mm, v(47.44, -17.28) * mm, v(45.78, -20.52) * mm, v(46.02, -20.76) * mm]});
            skFitSpline(sketch, "E512", {"points": [v(46.02, -20.76) * mm, v(46.54, -21.27) * mm, v(52.86, -21.2) * mm, v(58.59, -20.6) * mm]});
            skFitSpline(sketch, "E513", {"points": [v(127.35, -20.98) * mm, v(142.53, -19.68) * mm, v(158.85, -14.44) * mm, v(165.83, -8.62) * mm]});
            skFitSpline(sketch, "E514", {"points": [v(165.83, -7.55) * mm, v(164.06, -7.55) * mm, v(160.22, -8.2) * mm, v(150.39, -10.2) * mm]});
            skFitSpline(sketch, "E515", {"points": [v(150.39, -10.2) * mm, v(139.78, -12.34) * mm, v(134.86, -13.17) * mm, v(129.87, -13.67) * mm]});
            skFitSpline(sketch, "E516", {"points": [v(129.87, -13.67) * mm, v(126.12, -14.05) * mm, v(125.8, -14.12) * mm, v(124.1, -14.99) * mm]});
            skFitSpline(sketch, "E517", {"points": [v(124.1, -14.99) * mm, v(120.78, -16.69) * mm, v(114.28, -18.42) * mm, v(110.03, -18.75) * mm]});
            skFitSpline(sketch, "E518", {"points": [v(110.03, -18.75) * mm, v(108.92, -18.83) * mm, v(107.96, -18.98) * mm, v(107.9, -19.08) * mm]});
            skFitSpline(sketch, "E519", {"points": [v(107.9, -19.08) * mm, v(107.67, -19.46) * mm, v(113.39, -20.78) * mm, v(116.55, -21.06) * mm]});
            skFitSpline(sketch, "E520", {"points": [v(116.55, -21.06) * mm, v(118.68, -21.26) * mm, v(124.64, -21.21) * mm, v(127.35, -20.98) * mm]});
            skLineSegment(sketch, "E521", {"start": v(165.83, -8.62) * mm, "end": v(167.11, -7.55) * mm});
            skLineSegment(sketch, "E522", {"start": v(167.11, -7.55) * mm, "end": v(165.83, -7.55) * mm});
            skFitSpline(sketch, "E523", {"points": [v(-48.46, -16.55) * mm, v(-50.12, -13.2) * mm, v(-50.83, -12.46) * mm, v(-52.77, -11.96) * mm]});
            skFitSpline(sketch, "E524", {"points": [v(-52.77, -11.96) * mm, v(-54.9, -11.4) * mm, v(-60.37, -11.42) * mm, v(-64.17, -11.98) * mm]});
            skFitSpline(sketch, "E525", {"points": [v(-64.17, -11.98) * mm, v(-67.11, -12.42) * mm, v(-73.3, -13.83) * mm, v(-73.6, -14.14) * mm]});
            skFitSpline(sketch, "E526", {"points": [v(-73.6, -14.14) * mm, v(-73.7, -14.24) * mm, v(-73.56, -14.48) * mm, v(-73.3, -14.68) * mm]});
            skFitSpline(sketch, "E527", {"points": [v(-73.3, -14.68) * mm, v(-71.2, -16.28) * mm, v(-63.66, -18.14) * mm, v(-56.5, -18.83) * mm]});
            skFitSpline(sketch, "E528", {"points": [v(-56.5, -18.83) * mm, v(-51.35, -19.32) * mm, v(-49.56, -19.38) * mm, v(-48.16, -19.12) * mm]});
            skLineSegment(sketch, "E529", {"start": v(-48.16, -19.12) * mm, "end": v(-47.27, -18.95) * mm});
            skLineSegment(sketch, "E530", {"start": v(-47.27, -18.95) * mm, "end": v(-48.46, -16.55) * mm});
            skFitSpline(sketch, "E531", {"points": [v(101.3, -16.8) * mm, v(103.85, -16.44) * mm, v(108.04, -15.6) * mm, v(110.27, -14.97) * mm]});
            skFitSpline(sketch, "E532", {"points": [v(110.27, -14.97) * mm, v(111.18, -14.72) * mm, v(111.18, -14.71) * mm, v(110.75, -14.23) * mm]});
            skFitSpline(sketch, "E533", {"points": [v(110.75, -14.23) * mm, v(108.88, -12.16) * mm, v(101.57, -10.53) * mm, v(91.58, -9.94) * mm]});
            skFitSpline(sketch, "E534", {"points": [v(91.58, -9.94) * mm, v(86.6, -9.65) * mm, v(85.81, -9.72) * mm, v(84.54, -10.56) * mm]});
            skFitSpline(sketch, "E535", {"points": [v(84.54, -10.56) * mm, v(83.28, -11.38) * mm, v(79.87, -12.43) * mm, v(75.92, -13.2) * mm]});
            skFitSpline(sketch, "E536", {"points": [v(75.92, -13.2) * mm, v(73.76, -13.63) * mm, v(72.62, -13.96) * mm, v(72.83, -14.08) * mm]});
            skFitSpline(sketch, "E537", {"points": [v(72.83, -14.08) * mm, v(73.02, -14.18) * mm, v(74.3, -14.64) * mm, v(75.66, -15.1) * mm]});
            skFitSpline(sketch, "E538", {"points": [v(75.66, -15.1) * mm, v(78.39, -16.01) * mm, v(82.35, -16.79) * mm, v(86.07, -17.14) * mm]});
            skFitSpline(sketch, "E539", {"points": [v(86.07, -17.14) * mm, v(89.34, -17.44) * mm, v(97.93, -17.25) * mm, v(101.3, -16.8) * mm]});
            skFitSpline(sketch, "E540", {"points": [v(-115.7, -16.42) * mm, v(-111.87, -16) * mm, v(-107.53, -14.75) * mm, v(-109.9, -14.75) * mm]});
            skFitSpline(sketch, "E541", {"points": [v(-109.9, -14.75) * mm, v(-113.55, -14.75) * mm, v(-122.71, -12.02) * mm, v(-125.97, -9.96) * mm]});
            skFitSpline(sketch, "E542", {"points": [v(-125.97, -9.96) * mm, v(-126.88, -9.39) * mm, v(-127.56, -9.22) * mm, v(-130.22, -8.88) * mm]});
            skFitSpline(sketch, "E543", {"points": [v(-130.22, -8.88) * mm, v(-134.7, -8.32) * mm, v(-141.43, -6.93) * mm, v(-152.25, -4.32) * mm]});
            skFitSpline(sketch, "E544", {"points": [v(-152.25, -4.32) * mm, v(-162.68, -1.8) * mm, v(-165.07, -1.31) * mm, v(-166.84, -1.31) * mm]});
            skFitSpline(sketch, "E545", {"points": [v(-167.11, -2.15) * mm, v(-165.57, -3.54) * mm, v(-161.7, -6.06) * mm, v(-159, -7.42) * mm]});
            skFitSpline(sketch, "E546", {"points": [v(-159, -7.42) * mm, v(-152.12, -10.92) * mm, v(-141.95, -14.08) * mm, v(-132.7, -15.58) * mm]});
            skFitSpline(sketch, "E547", {"points": [v(-132.7, -15.58) * mm, v(-126.29, -16.63) * mm, v(-120.3, -16.92) * mm, v(-115.7, -16.42) * mm]});
            skLineSegment(sketch, "E548", {"start": v(-166.84, -1.31) * mm, "end": v(-168.05, -1.31) * mm});
            skLineSegment(sketch, "E549", {"start": v(-168.05, -1.31) * mm, "end": v(-167.11, -2.15) * mm});
            skFitSpline(sketch, "E550", {"points": [v(-83.97, -13.53) * mm, v(-82.59, -13.4) * mm, v(-80.43, -13.06) * mm, v(-79.17, -12.8) * mm]});
            skFitSpline(sketch, "E551", {"points": [v(-79.17, -12.8) * mm, v(-75.88, -12.08) * mm, v(-72.86, -10.91) * mm, v(-74.32, -10.91) * mm]});
            skFitSpline(sketch, "E552", {"points": [v(-74.32, -10.91) * mm, v(-74.6, -10.91) * mm, v(-76.5, -10.49) * mm, v(-78.53, -9.97) * mm]});
            skFitSpline(sketch, "E553", {"points": [v(-78.53, -9.97) * mm, v(-82.27, -9.02) * mm, v(-85.12, -7.91) * mm, v(-86.01, -7.07) * mm]});
            skFitSpline(sketch, "E554", {"points": [v(-86.01, -7.07) * mm, v(-86.7, -6.42) * mm, v(-91.05, -6.22) * mm, v(-96.57, -6.57) * mm]});
            skFitSpline(sketch, "E555", {"points": [v(-96.57, -6.57) * mm, v(-104.78, -7.1) * mm, v(-109.78, -8.2) * mm, v(-112.05, -9.94) * mm]});
            skFitSpline(sketch, "E556", {"points": [v(-111.93, -10.68) * mm, v(-110.5, -11.22) * mm, v(-106.83, -12.13) * mm, v(-103.77, -12.7) * mm]});
            skFitSpline(sketch, "E557", {"points": [v(-103.77, -12.7) * mm, v(-97.13, -13.93) * mm, v(-90.88, -14.19) * mm, v(-83.97, -13.53) * mm]});
            skLineSegment(sketch, "E558", {"start": v(-112.05, -9.94) * mm, "end": v(-112.65, -10.4) * mm});
            skLineSegment(sketch, "E559", {"start": v(-112.65, -10.4) * mm, "end": v(-111.93, -10.68) * mm});
            skLineSegment(sketch, "E560", {"start": v(-111.93, -10.68) * mm, "end": v(-112.05, -9.94) * mm});
            skFitSpline(sketch, "E561", {"points": [v(129.75, -11.28) * mm, v(143.45, -9.58) * mm, v(159.94, -3.96) * mm, v(169.59, 2.3) * mm]});
            skFitSpline(sketch, "E562", {"points": [v(169.59, 2.3) * mm, v(173.54, 4.87) * mm, v(175.72, 6.79) * mm, v(177.44, 9.23) * mm]});
            skFitSpline(sketch, "E563", {"points": [v(176.89, 9.52) * mm, v(166.15, 3.15) * mm, v(149.77, -1.6) * mm, v(130.35, -3.95) * mm]});
            skFitSpline(sketch, "E564", {"points": [v(130.35, -3.95) * mm, v(126.34, -4.44) * mm, v(126.1, -4.5) * mm, v(124.89, -5.3) * mm]});
            skFitSpline(sketch, "E565", {"points": [v(124.89, -5.3) * mm, v(122.47, -6.9) * mm, v(118.02, -8.5) * mm, v(114.5, -9) * mm]});
            skFitSpline(sketch, "E566", {"points": [v(114.5, -9) * mm, v(113.38, -9.17) * mm, v(112.38, -9.38) * mm, v(112.27, -9.48) * mm]});
            skFitSpline(sketch, "E567", {"points": [v(112.27, -9.48) * mm, v(111.96, -9.75) * mm, v(115.06, -10.89) * mm, v(117.1, -11.26) * mm]});
            skFitSpline(sketch, "E568", {"points": [v(117.1, -11.26) * mm, v(119.6, -11.7) * mm, v(126.2, -11.72) * mm, v(129.75, -11.28) * mm]});
            skLineSegment(sketch, "E569", {"start": v(177.44, 9.23) * mm, "end": v(178.19, 10.3) * mm});
            skLineSegment(sketch, "E570", {"start": v(178.19, 10.3) * mm, "end": v(176.89, 9.52) * mm});
            skLineSegment(sketch, "E571", {"start": v(176.89, 9.52) * mm, "end": v(177.44, 9.23) * mm});
            skFitSpline(sketch, "E572", {"points": [v(68.19, -10.9) * mm, v(73.7, -10.4) * mm, v(83.07, -8.67) * mm, v(83.07, -8.15) * mm]});
            skFitSpline(sketch, "E573", {"points": [v(83.07, -8.15) * mm, v(83.07, -7.38) * mm, v(80.77, -6.24) * mm, v(77.25, -5.29) * mm]});
            skFitSpline(sketch, "E574", {"points": [v(77.25, -5.29) * mm, v(75.12, -4.7) * mm, v(74.85, -4.68) * mm, v(72.49, -4.92) * mm]});
            skFitSpline(sketch, "E575", {"points": [v(72.49, -4.92) * mm, v(68.58, -5.31) * mm, v(65.44, -5.86) * mm, v(62.8, -6.6) * mm]});
            skFitSpline(sketch, "E576", {"points": [v(62.8, -6.6) * mm, v(60.13, -7.35) * mm, v(56.62, -8.76) * mm, v(55.74, -9.44) * mm]});
            skFitSpline(sketch, "E577", {"points": [v(56.68, -10.3) * mm, v(59.6, -11.12) * mm, v(63.51, -11.32) * mm, v(68.19, -10.9) * mm]});
            skLineSegment(sketch, "E578", {"start": v(55.74, -9.44) * mm, "end": v(55.17, -9.87) * mm});
            skLineSegment(sketch, "E579", {"start": v(55.17, -9.87) * mm, "end": v(56.68, -10.3) * mm});
            skFitSpline(sketch, "E580", {"points": [v(-59.86, -8.5) * mm, v(-58.94, -8.37) * mm, v(-57.77, -8.13) * mm, v(-57.26, -7.98) * mm]});
            skFitSpline(sketch, "E581", {"points": [v(-57.26, -7.98) * mm, v(-56.4, -7.72) * mm, v(-56.36, -7.68) * mm, v(-56.77, -7.37) * mm]});
            skFitSpline(sketch, "E582", {"points": [v(-56.77, -7.37) * mm, v(-59.47, -5.33) * mm, v(-66.87, -3.02) * mm, v(-73.38, -2.18) * mm]});
            skFitSpline(sketch, "E583", {"points": [v(-78.84, -2.5) * mm, v(-81.7, -3.23) * mm, v(-84.1, -4.32) * mm, v(-84.1, -4.9) * mm]});
            skFitSpline(sketch, "E584", {"points": [v(-84.1, -4.9) * mm, v(-84.1, -5.3) * mm, v(-82.33, -5.83) * mm, v(-77.13, -6.94) * mm]});
            skFitSpline(sketch, "E585", {"points": [v(-77.13, -6.94) * mm, v(-69.82, -8.51) * mm, v(-63.75, -9.06) * mm, v(-59.86, -8.5) * mm]});
            skLineSegment(sketch, "E586", {"start": v(-73.38, -2.18) * mm, "end": v(-76.11, -1.82) * mm});
            skLineSegment(sketch, "E587", {"start": v(-76.11, -1.82) * mm, "end": v(-78.84, -2.5) * mm});
            skLineSegment(sketch, "E588", {"start": v(-78.84, -2.5) * mm, "end": v(-73.38, -2.18) * mm});
            skFitSpline(sketch, "E589", {"points": [v(104.17, -7.9) * mm, v(107.38, -7.47) * mm, v(110.35, -6.84) * mm, v(112.7, -6.06) * mm]});
            skFitSpline(sketch, "E590", {"points": [v(103.7, -5.35) * mm, v(97.83, -5.27) * mm, v(91.73, -5.08) * mm, v(90.15, -4.94) * mm]});
            skFitSpline(sketch, "E591", {"points": [v(90.15, -4.94) * mm, v(85.76, -4.55) * mm, v(86.07, -4.47) * mm, v(86.91, -5.8) * mm]});
            skFitSpline(sketch, "E592", {"points": [v(86.91, -5.8) * mm, v(87.3, -6.42) * mm, v(87.63, -7.12) * mm, v(87.63, -7.35) * mm]});
            skFitSpline(sketch, "E593", {"points": [v(87.63, -7.35) * mm, v(87.63, -7.85) * mm, v(88.18, -7.98) * mm, v(91.7, -8.27) * mm]});
            skFitSpline(sketch, "E594", {"points": [v(91.7, -8.27) * mm, v(94.87, -8.53) * mm, v(100.59, -8.36) * mm, v(104.17, -7.9) * mm]});
            skLineSegment(sketch, "E595", {"start": v(112.7, -6.06) * mm, "end": v(114.39, -5.51) * mm});
            skLineSegment(sketch, "E596", {"start": v(114.39, -5.51) * mm, "end": v(103.7, -5.35) * mm});
            skFitSpline(sketch, "E597", {"points": [v(-118.41, -6.82) * mm, v(-116.8, -6.6) * mm, v(-112.89, -5.44) * mm, v(-113.08, -5.25) * mm]});
            skFitSpline(sketch, "E598", {"points": [v(-113.08, -5.25) * mm, v(-113.13, -5.2) * mm, v(-114.06, -4.99) * mm, v(-115.15, -4.78) * mm]});
            skFitSpline(sketch, "E599", {"points": [v(-115.15, -4.78) * mm, v(-119.07, -4.04) * mm, v(-123.48, -2.28) * mm, v(-125.97, -0.47) * mm]});
            skFitSpline(sketch, "E600", {"points": [v(-125.97, -0.47) * mm, v(-126.96, 0.25) * mm, v(-127.41, 0.37) * mm, v(-131.13, 0.96) * mm]});
            skFitSpline(sketch, "E601", {"points": [v(-131.13, 0.96) * mm, v(-149.72, 3.9) * mm, v(-166.04, 9.2) * mm, v(-176.22, 15.6) * mm]});
            skFitSpline(sketch, "E602", {"points": [v(-176.22, 15.6) * mm, v(-177.36, 16.3) * mm, v(-178.3, 16.83) * mm, v(-178.3, 16.76) * mm]});
            skFitSpline(sketch, "E603", {"points": [v(-178.3, 16.76) * mm, v(-178.3, 16.35) * mm, v(-175.96, 13.45) * mm, v(-174.65, 12.25) * mm]});
            skFitSpline(sketch, "E604", {"points": [v(-174.65, 12.25) * mm, v(-162.88, 1.33) * mm, v(-132.78, -8.87) * mm, v(-118.41, -6.82) * mm]});
            skFitSpline(sketch, "E605", {"points": [v(-89.2, -4.52) * mm, v(-88.96, -4.45) * mm, v(-88.77, -4.26) * mm, v(-88.77, -4.1) * mm]});
            skFitSpline(sketch, "E606", {"points": [v(-88.77, -4.1) * mm, v(-88.77, -3.92) * mm, v(-88.45, -3.3) * mm, v(-88.06, -2.73) * mm]});
            skFitSpline(sketch, "E607", {"points": [v(-88.06, -2.73) * mm, v(-87.67, -2.15) * mm, v(-87.34, -1.62) * mm, v(-87.34, -1.55) * mm]});
            skFitSpline(sketch, "E608", {"points": [v(-87.34, -1.55) * mm, v(-87.34, -1.49) * mm, v(-92.55, -1.42) * mm, v(-98.91, -1.41) * mm]});
            skFitSpline(sketch, "E609", {"points": [v(-98.91, -1.41) * mm, v(-105.28, -1.4) * mm, v(-111.63, -1.28) * mm, v(-113.01, -1.14) * mm]});
            skFitSpline(sketch, "E610", {"points": [v(-113.01, -1.14) * mm, v(-114.4, -1) * mm, v(-115.57, -0.92) * mm, v(-115.61, -0.96) * mm]});
            skFitSpline(sketch, "E611", {"points": [v(-115.61, -0.96) * mm, v(-115.65, -1) * mm, v(-114.84, -1.35) * mm, v(-113.81, -1.75) * mm]});
            skFitSpline(sketch, "E612", {"points": [v(-113.81, -1.75) * mm, v(-110.16, -3.14) * mm, v(-104.65, -4.25) * mm, v(-99.21, -4.66) * mm]});
            skFitSpline(sketch, "E613", {"points": [v(-99.21, -4.66) * mm, v(-96.68, -4.86) * mm, v(-90.06, -4.76) * mm, v(-89.2, -4.52) * mm]});
            skFitSpline(sketch, "E614", {"points": [v(91.67, 26.23) * mm, v(92.11, 33.2) * mm, v(92.55, 39.5) * mm, v(92.64, 40.24) * mm]});
            skFitSpline(sketch, "E615", {"points": [v(102.58, 51.26) * mm, v(107.95, 56.58) * mm, v(112.35, 61) * mm, v(112.35, 61.08) * mm]});
            skFitSpline(sketch, "E616", {"points": [v(112.35, 61.08) * mm, v(112.35, 61.17) * mm, v(110.86, 61.93) * mm, v(109.05, 62.77) * mm]});
            skFitSpline(sketch, "E617", {"points": [v(109.05, 62.77) * mm, v(107.23, 63.6) * mm, v(104.85, 64.71) * mm, v(103.76, 65.23) * mm]});
            skFitSpline(sketch, "E618", {"points": [v(103.76, 65.23) * mm, v(102.67, 65.74) * mm, v(101.68, 66.13) * mm, v(101.56, 66.09) * mm]});
            skFitSpline(sketch, "E619", {"points": [v(101.56, 66.09) * mm, v(101.44, 66.04) * mm, v(99.76, 63.96) * mm, v(97.82, 61.45) * mm]});
            skFitSpline(sketch, "E620", {"points": [v(97.82, 61.45) * mm, v(95.89, 58.94) * mm, v(93.54, 55.9) * mm, v(92.6, 54.67) * mm]});
            skFitSpline(sketch, "E621", {"points": [v(92.6, 54.67) * mm, v(91.66, 53.46) * mm, v(90.87, 52.49) * mm, v(90.84, 52.52) * mm]});
            skFitSpline(sketch, "E622", {"points": [v(90.84, 52.52) * mm, v(90.8, 52.55) * mm, v(90.93, 53.22) * mm, v(91.12, 54) * mm]});
            skFitSpline(sketch, "E623", {"points": [v(91.12, 54) * mm, v(91.36, 55.08) * mm, v(93.53, 66.98) * mm, v(93.93, 69.45) * mm]});
            skFitSpline(sketch, "E624", {"points": [v(93.93, 69.45) * mm, v(93.99, 69.78) * mm, v(82.94, 75.1) * mm, v(82.62, 74.9) * mm]});
            skFitSpline(sketch, "E625", {"points": [v(82.62, 74.9) * mm, v(82.53, 74.85) * mm, v(82.43, 74.44) * mm, v(82.4, 74) * mm]});
            skFitSpline(sketch, "E626", {"points": [v(82.4, 74) * mm, v(82.37, 73.57) * mm, v(82.24, 72.24) * mm, v(82.11, 71.05) * mm]});
            skFitSpline(sketch, "E627", {"points": [v(82.11, 71.05) * mm, v(81.99, 69.86) * mm, v(81.82, 68.24) * mm, v(81.75, 67.45) * mm]});
            skFitSpline(sketch, "E628", {"points": [v(81.75, 67.45) * mm, v(81.68, 66.66) * mm, v(81.51, 64.98) * mm, v(81.39, 63.71) * mm]});
            skFitSpline(sketch, "E629", {"points": [v(81.39, 63.71) * mm, v(81.26, 62.45) * mm, v(81.1, 60.72) * mm, v(81, 59.87) * mm]});
            skFitSpline(sketch, "E630", {"points": [v(81, 59.87) * mm, v(80.92, 59.02) * mm, v(80.62, 56.04) * mm, v(80.34, 53.25) * mm]});
            skLineSegment(sketch, "E631", {"start": v(92.64, 40.24) * mm, "end": v(92.82, 41.59) * mm});
            skLineSegment(sketch, "E632", {"start": v(92.82, 41.59) * mm, "end": v(102.58, 51.26) * mm});
            skFitSpline(sketch, "E633", {"points": [v(70.1, 38.17) * mm, v(64.76, 32.67) * mm, v(60.39, 28.05) * mm, v(60.39, 27.92) * mm]});
            skFitSpline(sketch, "E634", {"points": [v(60.39, 27.92) * mm, v(60.39, 27.7) * mm, v(70.4, 22.93) * mm, v(70.84, 22.93) * mm]});
            skFitSpline(sketch, "E635", {"points": [v(70.84, 22.93) * mm, v(71, 22.93) * mm, v(77.46, 30.94) * mm, v(80.56, 34.97) * mm]});
            skFitSpline(sketch, "E636", {"points": [v(80.56, 34.97) * mm, v(81.33, 35.99) * mm, v(82, 36.8) * mm, v(82.03, 36.76) * mm]});
            skFitSpline(sketch, "E637", {"points": [v(82.03, 36.76) * mm, v(82.07, 36.73) * mm, v(81.87, 35.4) * mm, v(81.6, 33.83) * mm]});
            skFitSpline(sketch, "E638", {"points": [v(81.6, 33.83) * mm, v(80.78, 29.07) * mm, v(79.49, 18.98) * mm, v(79.67, 18.79) * mm]});
            skFitSpline(sketch, "E639", {"points": [v(79.67, 18.79) * mm, v(79.84, 18.62) * mm, v(90.5, 13.6) * mm, v(90.75, 13.58) * mm]});
            skFitSpline(sketch, "E640", {"points": [v(90.75, 13.58) * mm, v(90.82, 13.57) * mm, v(91.23, 19.26) * mm, v(91.67, 26.23) * mm]});
            skLineSegment(sketch, "E641", {"start": v(80.34, 53.25) * mm, "end": v(79.83, 48.18) * mm});
            skLineSegment(sketch, "E642", {"start": v(79.83, 48.18) * mm, "end": v(70.1, 38.17) * mm});
            skFitSpline(sketch, "E643", {"points": [v(-85.8, 16.57) * mm, v(-85.04, 16.77) * mm, v(-83.88, 17.16) * mm, v(-83.24, 17.44) * mm]});
            skFitSpline(sketch, "E644", {"points": [v(-83.24, 17.44) * mm, v(-82.09, 17.93) * mm, v(-81.95, 17.94) * mm, v(-76.1, 17.66) * mm]});
            skFitSpline(sketch, "E645", {"points": [v(-76.1, 17.66) * mm, v(-72.82, 17.51) * mm, v(-68.7, 17.46) * mm, v(-66.97, 17.55) * mm]});
            skFitSpline(sketch, "E646", {"points": [v(-63.96, 22.54) * mm, v(-64.04, 25.2) * mm, v(-64.18, 27.44) * mm, v(-64.26, 27.52) * mm]});
            skFitSpline(sketch, "E647", {"points": [v(-64.26, 27.52) * mm, v(-64.35, 27.6) * mm, v(-65.98, 27.48) * mm, v(-67.9, 27.25) * mm]});
            skFitSpline(sketch, "E648", {"points": [v(-67.9, 27.25) * mm, v(-73.42, 26.56) * mm, v(-75.02, 26.45) * mm, v(-75.19, 26.73) * mm]});
            skFitSpline(sketch, "E649", {"points": [v(-75.19, 26.73) * mm, v(-75.27, 26.86) * mm, v(-75.24, 27.04) * mm, v(-75.1, 27.12) * mm]});
            skFitSpline(sketch, "E650", {"points": [v(-75.1, 27.12) * mm, v(-74.5, 27.5) * mm, v(-73.87, 30.5) * mm, v(-73.87, 33) * mm]});
            skFitSpline(sketch, "E651", {"points": [v(-73.87, 33) * mm, v(-73.88, 37.78) * mm, v(-75.54, 43.32) * mm, v(-79.05, 50.3) * mm]});
            skFitSpline(sketch, "E652", {"points": [v(-79.05, 50.3) * mm, v(-82.56, 57.28) * mm, v(-87.15, 62.9) * mm, v(-91.36, 65.38) * mm]});
            skFitSpline(sketch, "E653", {"points": [v(-91.36, 65.38) * mm, v(-95.27, 67.7) * mm, v(-99.4, 68.26) * mm, v(-103.3, 67) * mm]});
            skFitSpline(sketch, "E654", {"points": [v(-103.3, 67) * mm, v(-107.39, 65.68) * mm, v(-110.96, 62.75) * mm, v(-112.57, 59.4) * mm]});
            skFitSpline(sketch, "E655", {"points": [v(-112.57, 59.4) * mm, v(-114.08, 56.26) * mm, v(-114.33, 55) * mm, v(-114.32, 50.4) * mm]});
            skFitSpline(sketch, "E656", {"points": [v(-114.32, 50.4) * mm, v(-114.32, 46.85) * mm, v(-114.24, 45.99) * mm, v(-113.7, 43.69) * mm]});
            skFitSpline(sketch, "E657", {"points": [v(-113.7, 43.69) * mm, v(-110.7, 31.08) * mm, v(-101.55, 19.1) * mm, v(-93.05, 16.67) * mm]});
            skFitSpline(sketch, "E658", {"points": [v(-93.05, 16.67) * mm, v(-91.14, 16.13) * mm, v(-87.68, 16.08) * mm, v(-85.8, 16.57) * mm]});
            skLineSegment(sketch, "E659", {"start": v(-63.96, 22.54) * mm, "end": v(-66.97, 17.55) * mm});
            skFitSpline(sketch, "E660", {"points": [v(118.1, 26.74) * mm, v(117.41, 25.29) * mm, v(117, 24.9) * mm, v(116.6, 25.3) * mm]});
            skFitSpline(sketch, "E661", {"points": [v(116.6, 25.3) * mm, v(116.37, 25.52) * mm, v(116.54, 26.04) * mm, v(117.35, 27.62) * mm]});
            skFitSpline(sketch, "E662", {"points": [v(117.35, 27.62) * mm, v(117.92, 28.73) * mm, v(118.49, 29.65) * mm, v(118.61, 29.65) * mm]});
            skFitSpline(sketch, "E663", {"points": [v(118.61, 29.65) * mm, v(118.74, 29.65) * mm, v(119.7, 29.21) * mm, v(120.76, 28.68) * mm]});
            skFitSpline(sketch, "E664", {"points": [v(120.76, 28.68) * mm, v(121.82, 28.15) * mm, v(122.8, 27.78) * mm, v(122.93, 27.87) * mm]});
            skFitSpline(sketch, "E665", {"points": [v(122.93, 27.87) * mm, v(123.07, 27.95) * mm, v(123.82, 29.32) * mm, v(124.6, 30.9) * mm]});
            skFitSpline(sketch, "E666", {"points": [v(124.6, 30.9) * mm, v(126.78, 35.33) * mm, v(126.6, 36.05) * mm, v(122.82, 37.89) * mm]});
            skFitSpline(sketch, "E667", {"points": [v(122.82, 37.89) * mm, v(120.52, 39) * mm, v(119.51, 39.04) * mm, v(118.57, 38.03) * mm]});
            skFitSpline(sketch, "E668", {"points": [v(118.57, 38.03) * mm, v(117.52, 36.91) * mm, v(112.35, 26.47) * mm, v(112.35, 25.48) * mm]});
            skFitSpline(sketch, "E669", {"points": [v(112.35, 25.48) * mm, v(112.35, 24.41) * mm, v(113.17, 23.6) * mm, v(115.47, 22.43) * mm]});
            skFitSpline(sketch, "E670", {"points": [v(115.47, 22.43) * mm, v(117.83, 21.22) * mm, v(119, 21.17) * mm, v(119.9, 22.24) * mm]});
            skLineSegment(sketch, "E671", {"start": v(121.34, 24.6) * mm, "end": v(122.15, 26.2) * mm});
            skLineSegment(sketch, "E672", {"start": v(122.15, 26.2) * mm, "end": v(120.4, 27.07) * mm});
            skLineSegment(sketch, "E673", {"start": v(120.4, 27.07) * mm, "end": v(118.65, 27.93) * mm});
            skLineSegment(sketch, "E674", {"start": v(118.65, 27.93) * mm, "end": v(118.1, 26.74) * mm});
            skFitSpline(sketch, "E675", {"points": [v(114.9, 34.58) * mm, v(117.45, 39.59) * mm, v(119.54, 43.71) * mm, v(119.54, 43.74) * mm]});
            skFitSpline(sketch, "E676", {"points": [v(119.54, 43.74) * mm, v(119.55, 43.8) * mm, v(116.24, 45.49) * mm, v(116.12, 45.49) * mm]});
            skFitSpline(sketch, "E677", {"points": [v(116.12, 45.49) * mm, v(116.08, 45.49) * mm, v(115.62, 44.62) * mm, v(115.1, 43.57) * mm]});
            skFitSpline(sketch, "E678", {"points": [v(113.47, 42.37) * mm, v(112.47, 43.4) * mm, v(111.2, 43.73) * mm, v(110.24, 43.23) * mm]});
            skFitSpline(sketch, "E679", {"points": [v(110.24, 43.23) * mm, v(109.22, 42.7) * mm, v(108.5, 41.56) * mm, v(105.8, 36.25) * mm]});
            skFitSpline(sketch, "E680", {"points": [v(105.8, 36.25) * mm, v(103.37, 31.4) * mm, v(103, 30.3) * mm, v(103.45, 29.2) * mm]});
            skFitSpline(sketch, "E681", {"points": [v(103.45, 29.2) * mm, v(103.77, 28.42) * mm, v(105.27, 27.49) * mm, v(106.2, 27.49) * mm]});
            skFitSpline(sketch, "E682", {"points": [v(106.2, 27.49) * mm, v(106.55, 27.49) * mm, v(106.83, 27.35) * mm, v(106.83, 27.18) * mm]});
            skFitSpline(sketch, "E683", {"points": [v(106.83, 27.18) * mm, v(106.83, 26.86) * mm, v(109.65, 25.31) * mm, v(110.04, 25.41) * mm]});
            skFitSpline(sketch, "E684", {"points": [v(110.04, 25.41) * mm, v(110.16, 25.45) * mm, v(112.35, 29.57) * mm, v(114.9, 34.58) * mm]});
            skLineSegment(sketch, "E685", {"start": v(115.1, 43.57) * mm, "end": v(114.17, 41.65) * mm});
            skLineSegment(sketch, "E686", {"start": v(114.17, 41.65) * mm, "end": v(113.47, 42.37) * mm});
            skFitSpline(sketch, "E687", {"points": [v(58.92, 38.1) * mm, v(60.6, 43.29) * mm, v(63.4, 51.85) * mm, v(65.1, 57.13) * mm]});
            skFitSpline(sketch, "E688", {"points": [v(65.1, 57.13) * mm, v(66.82, 62.4) * mm, v(69.07, 69.32) * mm, v(70.12, 72.48) * mm]});
            skFitSpline(sketch, "E689", {"points": [v(70.12, 72.48) * mm, v(71.17, 75.64) * mm, v(71.94, 78.3) * mm, v(71.84, 78.4) * mm]});
            skFitSpline(sketch, "E690", {"points": [v(71.84, 78.4) * mm, v(71.75, 78.48) * mm, v(69.15, 79.36) * mm, v(66.07, 80.36) * mm]});
            skFitSpline(sketch, "E691", {"points": [v(66.07, 80.36) * mm, v(62.38, 81.54) * mm, v(60.44, 82.06) * mm, v(60.37, 81.88) * mm]});
            skFitSpline(sketch, "E692", {"points": [v(60.37, 81.88) * mm, v(59.73, 80.1) * mm, v(44.43, 32.76) * mm, v(44.43, 32.57) * mm]});
            skFitSpline(sketch, "E693", {"points": [v(44.43, 32.57) * mm, v(44.43, 32.42) * mm, v(45.8, 31.87) * mm, v(47.49, 31.34) * mm]});
            skFitSpline(sketch, "E694", {"points": [v(47.49, 31.34) * mm, v(49.17, 30.8) * mm, v(51.68, 30) * mm, v(53.07, 29.54) * mm]});
            skFitSpline(sketch, "E695", {"points": [v(53.07, 29.54) * mm, v(54.45, 29.08) * mm, v(55.65, 28.7) * mm, v(55.72, 28.7) * mm]});
            skFitSpline(sketch, "E696", {"points": [v(55.72, 28.7) * mm, v(55.8, 28.7) * mm, v(57.23, 32.93) * mm, v(58.92, 38.1) * mm]});
            skFitSpline(sketch, "E697", {"points": [v(101.73, 31.7) * mm, v(102.16, 32.55) * mm, v(102.5, 33.3) * mm, v(102.5, 33.37) * mm]});
            skFitSpline(sketch, "E698", {"points": [v(102.5, 33.37) * mm, v(102.5, 33.43) * mm, v(101.75, 33.86) * mm, v(100.83, 34.33) * mm]});
            skFitSpline(sketch, "E699", {"points": [v(98.3, 33.46) * mm, v(97.82, 32.53) * mm, v(97.47, 31.73) * mm, v(97.5, 31.7) * mm]});
            skFitSpline(sketch, "E700", {"points": [v(97.5, 31.7) * mm, v(97.74, 31.49) * mm, v(100.5, 30.15) * mm, v(100.71, 30.14) * mm]});
            skFitSpline(sketch, "E701", {"points": [v(100.71, 30.14) * mm, v(100.85, 30.13) * mm, v(101.3, 30.83) * mm, v(101.73, 31.7) * mm]});
            skLineSegment(sketch, "E702", {"start": v(100.83, 34.33) * mm, "end": v(99.15, 35.17) * mm});
            skLineSegment(sketch, "E703", {"start": v(99.15, 35.17) * mm, "end": v(98.3, 33.46) * mm});
            skFitSpline(sketch, "E704", {"points": [v(-47.7, 31.83) * mm, v(-41.4, 33.33) * mm, v(-37.48, 37.2) * mm, v(-36.31, 43.08) * mm]});
            skFitSpline(sketch, "E705", {"points": [v(-36.31, 43.08) * mm, v(-35.83, 45.52) * mm, v(-35.96, 50.57) * mm, v(-36.58, 53.4) * mm]});
            skFitSpline(sketch, "E706", {"points": [v(-36.58, 53.4) * mm, v(-36.94, 55.02) * mm, v(-46.02, 87.03) * mm, v(-46.17, 87.2) * mm]});
            skFitSpline(sketch, "E707", {"points": [v(-46.17, 87.2) * mm, v(-46.27, 87.3) * mm, v(-57.43, 84.1) * mm, v(-57.63, 83.91) * mm]});
            skFitSpline(sketch, "E708", {"points": [v(-57.63, 83.91) * mm, v(-57.73, 83.82) * mm, v(-55.6, 76.03) * mm, v(-52.9, 66.6) * mm]});
            skFitSpline(sketch, "E709", {"points": [v(-52.9, 66.6) * mm, v(-47.5, 47.83) * mm, v(-47.13, 46.19) * mm, v(-47.89, 44.17) * mm]});
            skFitSpline(sketch, "E710", {"points": [v(-47.89, 44.17) * mm, v(-48.27, 43.14) * mm, v(-48.5, 42.88) * mm, v(-49.48, 42.4) * mm]});
            skFitSpline(sketch, "E711", {"points": [v(-49.48, 42.4) * mm, v(-50.6, 41.84) * mm, v(-50.65, 41.84) * mm, v(-51.7, 42.24) * mm]});
            skFitSpline(sketch, "E712", {"points": [v(-51.7, 42.24) * mm, v(-53.02, 42.74) * mm, v(-53.83, 43.67) * mm, v(-54.85, 45.88) * mm]});
            skFitSpline(sketch, "E713", {"points": [v(-54.85, 45.88) * mm, v(-55.53, 47.34) * mm, v(-59.2, 59.73) * mm, v(-64.07, 76.93) * mm]});
            skFitSpline(sketch, "E714", {"points": [v(-64.07, 76.93) * mm, v(-64.76, 79.37) * mm, v(-65.4, 81.45) * mm, v(-65.48, 81.54) * mm]});
            skFitSpline(sketch, "E715", {"points": [v(-65.48, 81.54) * mm, v(-65.72, 81.82) * mm, v(-77.01, 78.53) * mm, v(-77.01, 78.18) * mm]});
            skFitSpline(sketch, "E716", {"points": [v(-77.01, 78.18) * mm, v(-77.02, 77.66) * mm, v(-67.92, 46.18) * mm, v(-67.25, 44.4) * mm]});
            skFitSpline(sketch, "E717", {"points": [v(-67.25, 44.4) * mm, v(-64.44, 36.9) * mm, v(-60.04, 32.24) * mm, v(-54.93, 31.35) * mm]});
            skFitSpline(sketch, "E718", {"points": [v(-54.93, 31.35) * mm, v(-53.18, 31.04) * mm, v(-50.18, 31.24) * mm, v(-47.7, 31.83) * mm]});
            skFitSpline(sketch, "E719", {"points": [v(28.67, 37.43) * mm, v(36.74, 38.98) * mm, v(42.26, 45.33) * mm, v(45, 56.24) * mm]});
            skFitSpline(sketch, "E720", {"points": [v(45, 56.24) * mm, v(46.79, 63.3) * mm, v(47.15, 70.56) * mm, v(45.98, 75.41) * mm]});
            skFitSpline(sketch, "E721", {"points": [v(45.98, 75.41) * mm, v(45.76, 76.31) * mm, v(45.1, 78.06) * mm, v(44.5, 79.3) * mm]});
            skFitSpline(sketch, "E722", {"points": [v(44.5, 79.3) * mm, v(43.6, 81.17) * mm, v(43.1, 81.88) * mm, v(41.46, 83.5) * mm]});
            skFitSpline(sketch, "E723", {"points": [v(41.46, 83.5) * mm, v(38.56, 86.38) * mm, v(35.84, 87.81) * mm, v(30.94, 89.03) * mm]});
            skFitSpline(sketch, "E724", {"points": [v(30.94, 89.03) * mm, v(26.98, 90) * mm, v(17.07, 91.03) * mm, v(17.06, 90.46) * mm]});
            skFitSpline(sketch, "E725", {"points": [v(17.06, 90.46) * mm, v(17.06, 90.34) * mm, v(16.9, 89.33) * mm, v(16.7, 88.2) * mm]});
            skFitSpline(sketch, "E726", {"points": [v(16.7, 88.2) * mm, v(16.5, 87.09) * mm, v(16.18, 85.3) * mm, v(16, 84.25) * mm]});
            skFitSpline(sketch, "E727", {"points": [v(16, 84.25) * mm, v(15.8, 83.2) * mm, v(15.22, 79.9) * mm, v(14.7, 76.93) * mm]});
            skFitSpline(sketch, "E728", {"points": [v(14.7, 76.93) * mm, v(14.16, 73.96) * mm, v(13.45, 69.9) * mm, v(13.1, 67.93) * mm]});
            skFitSpline(sketch, "E729", {"points": [v(13.1, 67.93) * mm, v(12.76, 65.95) * mm, v(12.31, 63.4) * mm, v(12.12, 62.29) * mm]});
            skFitSpline(sketch, "E730", {"points": [v(12.12, 62.29) * mm, v(11.92, 61.17) * mm, v(11.5, 58.79) * mm, v(11.19, 57) * mm]});
            skFitSpline(sketch, "E731", {"points": [v(11.19, 57) * mm, v(10.16, 51.16) * mm, v(9.15, 45.41) * mm, v(8.67, 42.73) * mm]});
            skFitSpline(sketch, "E732", {"points": [v(8.67, 42.73) * mm, v(8.41, 41.28) * mm, v(8.28, 40.02) * mm, v(8.37, 39.93) * mm]});
            skFitSpline(sketch, "E733", {"points": [v(8.37, 39.93) * mm, v(8.82, 39.51) * mm, v(16.94, 37.65) * mm, v(20.07, 37.25) * mm]});
            skFitSpline(sketch, "E734", {"points": [v(20.07, 37.25) * mm, v(21.96, 37) * mm, v(27.02, 37.12) * mm, v(28.67, 37.43) * mm]});
            skFitSpline(sketch, "E735", {"points": [v(-23.67, 38.14) * mm, v(-21.2, 38.31) * mm, v(-19.13, 38.5) * mm, v(-19.07, 38.55) * mm]});
            skFitSpline(sketch, "E736", {"points": [v(-19.07, 38.55) * mm, v(-19.01, 38.61) * mm, v(-18.73, 40.92) * mm, v(-18.44, 43.7) * mm]});
            skFitSpline(sketch, "E737", {"points": [v(-18.44, 43.7) * mm, v(-18.15, 46.46) * mm, v(-17.9, 48.76) * mm, v(-17.86, 48.8) * mm]});
            skFitSpline(sketch, "E738", {"points": [v(-17.86, 48.8) * mm, v(-17.73, 48.94) * mm, v(-9.8, 49.4) * mm, v(-9.67, 49.27) * mm]});
            skFitSpline(sketch, "E739", {"points": [v(-9.67, 49.27) * mm, v(-9.6, 49.19) * mm, v(-9.02, 46.95) * mm, v(-8.39, 44.3) * mm]});
            skFitSpline(sketch, "E740", {"points": [v(-8.39, 44.3) * mm, v(-7.76, 41.65) * mm, v(-7.2, 39.44) * mm, v(-7.15, 39.39) * mm]});
            skFitSpline(sketch, "E741", {"points": [v(-7.15, 39.39) * mm, v(-7.05, 39.28) * mm, v(3.8, 39.96) * mm, v(4.27, 40.1) * mm]});
            skFitSpline(sketch, "E742", {"points": [v(4.27, 40.1) * mm, v(4.47, 40.15) * mm, v(4.27, 41.24) * mm, v(3.63, 43.73) * mm]});
            skFitSpline(sketch, "E743", {"points": [v(3.63, 43.73) * mm, v(2.25, 49) * mm, v(-8.04, 89.37) * mm, v(-8.3, 90.49) * mm]});
            skFitSpline(sketch, "E744", {"points": [v(-10.67, 91.4) * mm, v(-13.56, 91.36) * mm, v(-23.03, 90.67) * mm, v(-23.2, 90.5) * mm]});
            skFitSpline(sketch, "E745", {"points": [v(-23.2, 90.5) * mm, v(-23.33, 90.38) * mm, v(-24.21, 84.24) * mm, v(-26.74, 66) * mm]});
            skFitSpline(sketch, "E746", {"points": [v(-26.74, 66) * mm, v(-27.21, 62.58) * mm, v(-27.97, 57.18) * mm, v(-28.41, 54) * mm]});
            skFitSpline(sketch, "E747", {"points": [v(-28.41, 54) * mm, v(-28.86, 50.84) * mm, v(-29.51, 46.2) * mm, v(-29.85, 43.69) * mm]});
            skFitSpline(sketch, "E748", {"points": [v(-29.85, 43.69) * mm, v(-30.2, 41.18) * mm, v(-30.54, 38.78) * mm, v(-30.6, 38.36) * mm]});
            skLineSegment(sketch, "E749", {"start": v(-8.3, 90.49) * mm, "end": v(-8.52, 91.45) * mm});
            skLineSegment(sketch, "E750", {"start": v(-8.52, 91.45) * mm, "end": v(-10.67, 91.4) * mm});
            skLineSegment(sketch, "E751", {"start": v(-10.67, 91.4) * mm, "end": v(-8.3, 90.49) * mm});
            skFitSpline(sketch, "E752", {"points": [v(-29.46, 37.72) * mm, v(-28.75, 37.78) * mm, v(-26.15, 37.97) * mm, v(-23.67, 38.14) * mm]});
            skLineSegment(sketch, "E753", {"start": v(-30.6, 38.36) * mm, "end": v(-30.74, 37.6) * mm});
            skLineSegment(sketch, "E754", {"start": v(-30.74, 37.6) * mm, "end": v(-29.46, 37.72) * mm});
            skLineSegment(sketch, "E755", {"start": v(-29.46, 37.72) * mm, "end": v(-30.6, 38.36) * mm});
            skLineSegment(sketch, "E756", {"start": v(119.9, 22.24) * mm, "end": v(121.34, 24.6) * mm});
            skLineSegment(sketch, "E757", {"start": v(-120.23, 7.4) * mm, "end": v(-119.85, 3.5) * mm});
            skLineSegment(sketch, "E758", {"start": v(-112.94, 7.12) * mm, "end": v(-112.94, 3.07) * mm});
            skLineSegment(sketch, "E759", {"start": v(-99.2, 7.37) * mm, "end": v(-112.94, 7.12) * mm});
            skLineSegment(sketch, "E760", {"start": v(115.61, 2.85) * mm, "end": v(115.77, -1.2) * mm});
            skLineSegment(sketch, "E761", {"start": v(107.75, 3.13) * mm, "end": v(107.75, -1.32) * mm});
            skFitSpline(sketch, "E762.trimOffspring", {"points": [v(124.95, 2.85) * mm, v(116.78, 2.7) * mm, v(111.02, 2.88) * mm, v(96.75, 3.74) * mm]});
            skLineSegment(sketch, "E763", {"start": v(34.67, -28.43) * mm, "end": v(37.95, -26.51) * mm});
            skLineSegment(sketch, "E764", {"start": v(34.67, -31.9) * mm, "end": v(37.77, -30.05) * mm});
            skLineSegment(sketch, "E765", {"start": v(-36.35, -24.93) * mm, "end": v(-39.83, -24.6) * mm});
            skLineSegment(sketch, "E766", {"start": v(-39.72, -27.03) * mm, "end": v(-36.67, -27.83) * mm});
            skSolve(sketch);
        }
        {
            var Q0;
            Q0=makeQuery(id+"F0.imprint","IMPRINT",FACE,{"disambiguationData":[TD([[makeQuery(id+"F0.imprint","IMPRINT",EDGE,{"derivedFrom":sQuery(id+"F0.wireOp",EDGE,"E0")}),-1.0]])]});
            extrude(context, id + "F1", {"entities" : qUnion([Q0]), "depth" : 20 * mm});
        }
    });
